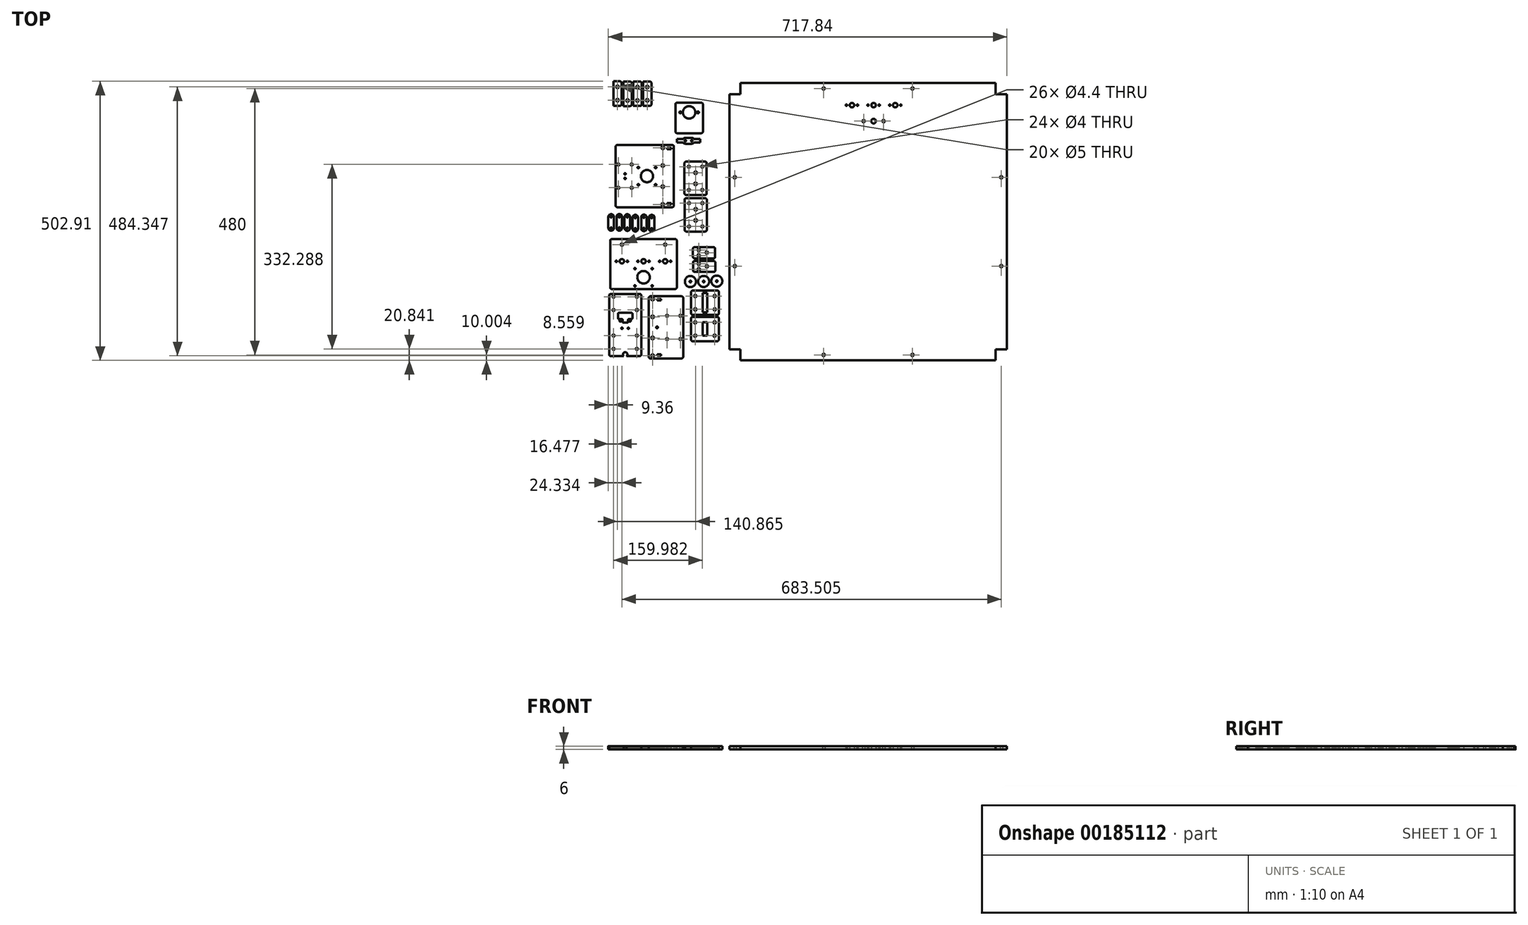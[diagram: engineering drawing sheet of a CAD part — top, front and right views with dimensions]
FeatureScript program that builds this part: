
annotation { "Feature Type Name" : "Feature", "Feature Type Description" : "" }
export const myFeature = defineFeature(function(context is Context, id is Id, definition is map)
    precondition{}
    {
        {
            var Q0;
            Q0=qCreatedBy(makeId("Top.planeOp"),FACE);
            var sketch = newSketch(context, id + "F0", { "sketchPlane" : qUnion([Q0])});
            skLineSegment(sketch, "E0.bottom", {"start": v(-220.47, 123.7) * mm, "end": v(-121.47, 123.7) * mm});
            skLineSegment(sketch, "E0.top", {"start": v(-220.47, 11.7) * mm, "end": v(-121.47, 11.7) * mm});
            skLineSegment(sketch, "E0.left", {"start": v(-223.47, 120.7) * mm, "end": v(-223.47, 14.7) * mm});
            skLineSegment(sketch, "E0.right", {"start": v(-118.47, 120.7) * mm, "end": v(-118.47, 14.7) * mm});
            skCircle(sketch, "E1", {"center": v(-218.47, 88.7) * mm, "radius": 2 * mm});
            skCircle(sketch, "E2", {"center": v(-218.47, 46.7) * mm, "radius": 2 * mm});
            skCircle(sketch, "E3", {"center": v(-194.47, 88.7) * mm, "radius": 2 * mm});
            skCircle(sketch, "E4", {"center": v(-182.47, 83.2) * mm, "radius": 1.4 * mm});
            skCircle(sketch, "E5", {"center": v(-151.47, 83.2) * mm, "radius": 1.4 * mm});
            skCircle(sketch, "E6", {"center": v(-151.47, 52.2) * mm, "radius": 1.4 * mm});
            skCircle(sketch, "E7", {"center": v(-182.47, 52.2) * mm, "radius": 1.4 * mm});
            skCircle(sketch, "E8", {"center": v(-166.97, 67.7) * mm, "radius": 11.1 * mm});
            skCircle(sketch, "E9", {"center": v(-194.47, 46.7) * mm, "radius": 2 * mm});
            skCircle(sketch, "E10", {"center": v(-138.47, 118.7) * mm, "radius": 2.5 * mm});
            skCircle(sketch, "E11", {"center": v(-138.47, 86.7) * mm, "radius": 2.5 * mm});
            skCircle(sketch, "E12", {"center": v(-138.47, 48.7) * mm, "radius": 2.5 * mm});
            skCircle(sketch, "E13", {"center": v(-138.47, 16.7) * mm, "radius": 2.5 * mm});
            skCircle(sketch, "E14", {"center": v(-206.47, 71.7) * mm, "radius": 1.3 * mm});
            skCircle(sketch, "E15", {"center": v(-206.47, 63.7) * mm, "radius": 1.3 * mm});
            skLineSegment(sketch, "E16.bottom", {"start": v(-130.47, 118.7) * mm, "end": v(-123.47, 118.7) * mm});
            skLineSegment(sketch, "E16.top", {"start": v(-130.47, 116.2) * mm, "end": v(-123.47, 116.2) * mm});
            skLineSegment(sketch, "E16.left", {"start": v(-130.47, 118.7) * mm, "end": v(-130.47, 116.2) * mm});
            skLineSegment(sketch, "E16.right", {"start": v(-123.47, 118.7) * mm, "end": v(-123.47, 116.2) * mm});
            skLineSegment(sketch, "E17.bottom", {"start": v(-130.47, 19.2) * mm, "end": v(-123.47, 19.2) * mm});
            skLineSegment(sketch, "E17.top", {"start": v(-130.47, 16.7) * mm, "end": v(-123.47, 16.7) * mm});
            skLineSegment(sketch, "E17.left", {"start": v(-130.47, 19.2) * mm, "end": v(-130.47, 16.7) * mm});
            skLineSegment(sketch, "E17.right", {"start": v(-123.47, 19.2) * mm, "end": v(-123.47, 16.7) * mm});
            skPoint(sketch, "E18.visualSharp", {"position": v(-118.47, 123.7) * mm});
            skArc(sketch, "E18.filletArc", {"start": v(-118.47, 120.7) * mm, "mid": v(-119.35, 122.83) * mm, "end": v(-121.47, 123.7) * mm});
            skPoint(sketch, "E19.visualSharp", {"position": v(-223.47, 123.7) * mm});
            skArc(sketch, "E19.filletArc", {"start": v(-220.47, 123.7) * mm, "mid": v(-222.6, 122.83) * mm, "end": v(-223.47, 120.7) * mm});
            skPoint(sketch, "E20.visualSharp", {"position": v(-223.47, 11.7) * mm});
            skArc(sketch, "E20.filletArc", {"start": v(-223.47, 14.7) * mm, "mid": v(-222.6, 12.59) * mm, "end": v(-220.47, 11.7) * mm});
            skPoint(sketch, "E21.visualSharp", {"position": v(-118.47, 11.7) * mm});
            skArc(sketch, "E21.filletArc", {"start": v(-121.47, 11.7) * mm, "mid": v(-119.35, 12.59) * mm, "end": v(-118.47, 14.7) * mm});
            skSolve(sketch);
        }
        {
            var Q0;
            Q0 = qSketchRegion(id + "F0", true);
            extrude(context, id + "F1", {"entities" : qUnion([Q0]), "depth" : 6 * mm});
        }
        {
            var Q0;
            Q0=qCreatedBy(makeId("Top.planeOp"),FACE);
            var sketch = newSketch(context, id + "F2", { "sketchPlane" : qUnion([Q0])});
            skLineSegment(sketch, "E22.bottom", {"start": v(127.2, 102.14) * mm, "end": v(183.2, 102.14) * mm});
            skLineSegment(sketch, "E22.top", {"start": v(127.2, -9.86) * mm, "end": v(183.2, -9.86) * mm});
            skLineSegment(sketch, "E22.left", {"start": v(124.2, 99.14) * mm, "end": v(124.2, -6.86) * mm});
            skLineSegment(sketch, "E22.right", {"start": v(186.2, 99.14) * mm, "end": v(186.2, -6.86) * mm});
            skCircle(sketch, "E23", {"center": v(157.2, 67.14) * mm, "radius": 2 * mm});
            skCircle(sketch, "E24", {"center": v(157.2, 25.14) * mm, "radius": 2 * mm});
            skCircle(sketch, "E25", {"center": v(181.2, 67.14) * mm, "radius": 2 * mm});
            skCircle(sketch, "E26", {"center": v(181.2, 25.14) * mm, "radius": 2 * mm});
            skCircle(sketch, "E27", {"center": v(131.2, 97.14) * mm, "radius": 2.5 * mm});
            skCircle(sketch, "E28", {"center": v(131.2, 65.14) * mm, "radius": 2.5 * mm});
            skCircle(sketch, "E29", {"center": v(131.2, 27.14) * mm, "radius": 2.5 * mm});
            skCircle(sketch, "E30", {"center": v(131.2, -4.86) * mm, "radius": 2.5 * mm});
            skLineSegment(sketch, "E31.bottom", {"start": v(139.2, 97.14) * mm, "end": v(146.2, 97.14) * mm});
            skLineSegment(sketch, "E31.top", {"start": v(139.2, 94.64) * mm, "end": v(146.2, 94.64) * mm});
            skLineSegment(sketch, "E31.left", {"start": v(139.2, 97.14) * mm, "end": v(139.2, 94.64) * mm});
            skLineSegment(sketch, "E31.right", {"start": v(146.2, 97.14) * mm, "end": v(146.2, 94.64) * mm});
            skLineSegment(sketch, "E32.bottom", {"start": v(139.2, -2.36) * mm, "end": v(146.2, -2.36) * mm});
            skLineSegment(sketch, "E32.top", {"start": v(139.2, -4.86) * mm, "end": v(146.2, -4.86) * mm});
            skLineSegment(sketch, "E32.left", {"start": v(139.2, -2.36) * mm, "end": v(139.2, -4.86) * mm});
            skLineSegment(sketch, "E32.right", {"start": v(146.2, -2.36) * mm, "end": v(146.2, -4.86) * mm});
            skPoint(sketch, "E33.visualSharp", {"position": v(124.2, 102.14) * mm});
            skArc(sketch, "E33.filletArc", {"start": v(127.2, 102.14) * mm, "mid": v(125.08, 101.26) * mm, "end": v(124.2, 99.14) * mm});
            skPoint(sketch, "E34.visualSharp", {"position": v(186.2, 102.14) * mm});
            skArc(sketch, "E34.filletArc", {"start": v(186.2, 99.14) * mm, "mid": v(185.32, 101.26) * mm, "end": v(183.2, 102.14) * mm});
            skPoint(sketch, "E35.visualSharp", {"position": v(186.2, -9.86) * mm});
            skArc(sketch, "E35.filletArc", {"start": v(183.2, -9.86) * mm, "mid": v(185.32, -8.98) * mm, "end": v(186.2, -6.86) * mm});
            skPoint(sketch, "E36.visualSharp", {"position": v(124.2, -9.86) * mm});
            skArc(sketch, "E36.filletArc", {"start": v(124.2, -6.86) * mm, "mid": v(125.08, -8.98) * mm, "end": v(127.2, -9.86) * mm});
            skCircle(sketch, "E37", {"center": v(139.2, 46.14) * mm, "radius": 1.5 * mm});
            skSolve(sketch);
        }
        {
            var Q0;
            Q0 = qSketchRegion(id + "F2", true);
            extrude(context, id + "F3", {"entities" : qUnion([Q0]), "depth" : 6 * mm});
        }
        {
            var Q0;
            Q0=qCreatedBy(makeId("Top.planeOp"),FACE);
            var sketch = newSketch(context, id + "F4", { "sketchPlane" : qUnion([Q0])});
            skLineSegment(sketch, "E38.bottom", {"start": v(-34.17, 117.42) * mm, "end": v(17.83, 117.42) * mm});
            skLineSegment(sketch, "E38.top", {"start": v(-34.17, 5.42) * mm, "end": v(-10.82, 5.42) * mm});
            skLineSegment(sketch, "E38.left", {"start": v(-37.17, 114.42) * mm, "end": v(-37.17, 8.42) * mm});
            skLineSegment(sketch, "E38.right", {"start": v(20.83, 114.42) * mm, "end": v(20.83, 67.93) * mm});
            skCircle(sketch, "E39", {"center": v(-29.17, 112.42) * mm, "radius": 2 * mm});
            skCircle(sketch, "E40", {"center": v(-29.17, 88.42) * mm, "radius": 2 * mm});
            skCircle(sketch, "E41", {"center": v(12.83, 112.42) * mm, "radius": 2 * mm});
            skCircle(sketch, "E42", {"center": v(12.83, 88.42) * mm, "radius": 2 * mm});
            skCircle(sketch, "E43", {"center": v(-29.17, 42.42) * mm, "radius": 2 * mm});
            skCircle(sketch, "E44", {"center": v(-29.17, 18.42) * mm, "radius": 2 * mm});
            skCircle(sketch, "E45", {"center": v(12.83, 42.42) * mm, "radius": 2 * mm});
            skCircle(sketch, "E46", {"center": v(12.83, 18.42) * mm, "radius": 2 * mm});
            skCircle(sketch, "E47", {"center": v(-16.97, 68.92) * mm, "radius": 1.5 * mm});
            skCircle(sketch, "E48", {"center": v(0.63, 68.92) * mm, "radius": 1.5 * mm});
            skLineSegment(sketch, "E49.bottom", {"start": v(-19.17, 83.42) * mm, "end": v(2.83, 83.42) * mm});
            skLineSegment(sketch, "E49.top", {"start": v(-19.17, 71.92) * mm, "end": v(-13.97, 71.92) * mm});
            skLineSegment(sketch, "E49.left", {"start": v(-21.17, 81.42) * mm, "end": v(-21.17, 73.92) * mm});
            skLineSegment(sketch, "E49.right", {"start": v(4.83, 81.42) * mm, "end": v(4.83, 73.92) * mm});
            skPoint(sketch, "E50.visualSharp", {"position": v(-37.17, 117.42) * mm});
            skArc(sketch, "E50.filletArc", {"start": v(-34.17, 117.42) * mm, "mid": v(-36.3, 116.54) * mm, "end": v(-37.17, 114.42) * mm});
            skPoint(sketch, "E51.visualSharp", {"position": v(20.83, 117.42) * mm});
            skArc(sketch, "E51.filletArc", {"start": v(20.83, 114.42) * mm, "mid": v(19.95, 116.54) * mm, "end": v(17.83, 117.42) * mm});
            skPoint(sketch, "E52.visualSharp", {"position": v(20.83, 5.42) * mm});
            skArc(sketch, "E52.filletArc", {"start": v(17.83, 5.42) * mm, "mid": v(19.95, 6.3) * mm, "end": v(20.83, 8.42) * mm});
            skPoint(sketch, "E53.visualSharp", {"position": v(-37.17, 5.42) * mm});
            skArc(sketch, "E53.filletArc", {"start": v(-37.17, 8.42) * mm, "mid": v(-36.3, 6.3) * mm, "end": v(-34.17, 5.42) * mm});
            skPoint(sketch, "E54.visualSharp", {"position": v(4.83, 83.42) * mm});
            skArc(sketch, "E54.filletArc", {"start": v(4.83, 81.42) * mm, "mid": v(4.24, 82.84) * mm, "end": v(2.83, 83.42) * mm});
            skPoint(sketch, "E55.visualSharp", {"position": v(4.83, 71.92) * mm});
            skArc(sketch, "E55.filletArc", {"start": v(2.83, 71.92) * mm, "mid": v(4.24, 72.5) * mm, "end": v(4.83, 73.92) * mm});
            skPoint(sketch, "E56.visualSharp", {"position": v(-21.17, 71.92) * mm});
            skArc(sketch, "E56.filletArc", {"start": v(-21.17, 73.92) * mm, "mid": v(-20.58, 72.5) * mm, "end": v(-19.17, 71.92) * mm});
            skPoint(sketch, "E57.visualSharp", {"position": v(-21.17, 83.42) * mm});
            skArc(sketch, "E57.filletArc", {"start": v(-19.17, 83.42) * mm, "mid": v(-20.58, 82.84) * mm, "end": v(-21.17, 81.42) * mm});
            skCircle(sketch, "E58", {"center": v(-13.97, 55.42) * mm, "radius": 1.3 * mm});
            skCircle(sketch, "E59", {"center": v(-2.37, 55.42) * mm, "radius": 1.3 * mm});
            skLineSegment(sketch, "E60.trimOffspring", {"start": v(20.83, 59.08) * mm, "end": v(20.83, 8.42) * mm});
            skLineSegment(sketch, "E61.top", {"start": v(-11.97, 65.92) * mm, "end": v(-3.97, 65.92) * mm});
            skLineSegment(sketch, "E61.left", {"start": v(-12.97, 70.92) * mm, "end": v(-12.97, 66.92) * mm});
            skLineSegment(sketch, "E61.right", {"start": v(-2.97, 70.92) * mm, "end": v(-2.97, 66.92) * mm});
            skLineSegment(sketch, "E62.trimOffspring", {"start": v(-1.97, 71.92) * mm, "end": v(2.83, 71.92) * mm});
            skPoint(sketch, "E63.visualSharp", {"position": v(-12.97, 71.92) * mm});
            skArc(sketch, "E63.filletArc", {"start": v(-12.97, 70.92) * mm, "mid": v(-13.26, 71.63) * mm, "end": v(-13.97, 71.92) * mm});
            skPoint(sketch, "E64.visualSharp", {"position": v(-2.97, 71.92) * mm});
            skArc(sketch, "E64.filletArc", {"start": v(-1.97, 71.92) * mm, "mid": v(-2.68, 71.63) * mm, "end": v(-2.97, 70.92) * mm});
            skPoint(sketch, "E65.visualSharp", {"position": v(-12.97, 65.92) * mm});
            skArc(sketch, "E65.filletArc", {"start": v(-12.97, 66.92) * mm, "mid": v(-12.68, 66.21) * mm, "end": v(-11.97, 65.92) * mm});
            skPoint(sketch, "E66.visualSharp", {"position": v(-2.97, 65.92) * mm});
            skArc(sketch, "E66.filletArc", {"start": v(-3.97, 65.92) * mm, "mid": v(-3.26, 66.21) * mm, "end": v(-2.97, 66.92) * mm});
            skLineSegment(sketch, "E67", {"start": v(20.83, 59.08) * mm, "end": v(20.83, 67.93) * mm});
            skArc(sketch, "E68", {"start": v(-5.52, 5.42) * mm, "mid": v(-8.17, 12.42) * mm, "end": v(-10.82, 5.42) * mm});
            skPoint(sketch, "E68.centerSnap0", {"position": v(-8.17, 5.42) * mm});
            skLineSegment(sketch, "E69.trimOffspring", {"start": v(-5.52, 5.42) * mm, "end": v(17.83, 5.42) * mm});
            skSolve(sketch);
        }
        {
            var Q0;
            Q0=makeQuery(id+"F4.imprint","IMPRINT",FACE,{"disambiguationData":[TD([[makeQuery(id+"F4.imprint","IMPRINT",EDGE,{"derivedFrom":sQuery(id+"F4.wireOp",EDGE,"E38.bottom")}),-1.0]])]});
            extrude(context, id + "F5", {"entities" : qUnion([Q0]), "depth" : 6 * mm});
        }
        {
            var Q0;
            Q0=qCreatedBy(makeId("Top.planeOp"),FACE);
            var sketch = newSketch(context, id + "F6", { "sketchPlane" : qUnion([Q0])});
            skLineSegment(sketch, "E70.bottom", {"start": v(-96.37, 93.78) * mm, "end": v(-62.37, 93.78) * mm});
            skLineSegment(sketch, "E70.top", {"start": v(-96.37, 33.78) * mm, "end": v(-62.37, 33.78) * mm});
            skLineSegment(sketch, "E70.left", {"start": v(-99.37, 90.78) * mm, "end": v(-99.37, 36.78) * mm});
            skLineSegment(sketch, "E70.right", {"start": v(-59.37, 90.78) * mm, "end": v(-59.37, 36.78) * mm});
            skCircle(sketch, "E71", {"center": v(-91.37, 84.78) * mm, "radius": 2 * mm});
            skCircle(sketch, "E72", {"center": v(-67.37, 84.78) * mm, "radius": 2 * mm});
            skCircle(sketch, "E73", {"center": v(-91.37, 42.78) * mm, "radius": 2 * mm});
            skCircle(sketch, "E74", {"center": v(-67.37, 42.78) * mm, "radius": 2 * mm});
            skCircle(sketch, "E75", {"center": v(-79.37, 73.78) * mm, "radius": 2.5 * mm});
            skCircle(sketch, "E76", {"center": v(-79.37, 53.78) * mm, "radius": 2.5 * mm});
            skPoint(sketch, "E77.visualSharp", {"position": v(-99.37, 93.78) * mm});
            skArc(sketch, "E77.filletArc", {"start": v(-96.37, 93.78) * mm, "mid": v(-98.49, 92.9) * mm, "end": v(-99.37, 90.78) * mm});
            skPoint(sketch, "E78.visualSharp", {"position": v(-59.37, 93.78) * mm});
            skArc(sketch, "E78.filletArc", {"start": v(-59.37, 90.78) * mm, "mid": v(-60.24, 92.9) * mm, "end": v(-62.37, 93.78) * mm});
            skPoint(sketch, "E79.visualSharp", {"position": v(-59.37, 33.78) * mm});
            skArc(sketch, "E79.filletArc", {"start": v(-62.37, 33.78) * mm, "mid": v(-60.24, 34.65) * mm, "end": v(-59.37, 36.78) * mm});
            skPoint(sketch, "E80.visualSharp", {"position": v(-99.37, 33.78) * mm});
            skArc(sketch, "E80.filletArc", {"start": v(-99.37, 36.78) * mm, "mid": v(-98.49, 34.65) * mm, "end": v(-96.37, 33.78) * mm});
            skSolve(sketch);
        }
        {
            var Q0;
            Q0 = qSketchRegion(id + "F6", true);
            extrude(context, id + "F7", {"entities" : qUnion([Q0]), "depth" : 6 * mm});
        }
        {
            var Q0;
            Q0=qCreatedBy(makeId("Top.planeOp"),FACE);
            var sketch = newSketch(context, id + "F8", { "sketchPlane" : qUnion([Q0])});
            skLineSegment(sketch, "E81.bottom", {"start": v(-96.19, 27.94) * mm, "end": v(-62.19, 27.94) * mm});
            skLineSegment(sketch, "E81.top", {"start": v(-96.19, -32.06) * mm, "end": v(-62.19, -32.06) * mm});
            skLineSegment(sketch, "E81.left", {"start": v(-99.19, 24.94) * mm, "end": v(-99.19, -29.06) * mm});
            skLineSegment(sketch, "E81.right", {"start": v(-59.19, 24.94) * mm, "end": v(-59.19, -29.06) * mm});
            skCircle(sketch, "E82", {"center": v(-91.19, 18.94) * mm, "radius": 2 * mm});
            skCircle(sketch, "E83", {"center": v(-67.19, 18.94) * mm, "radius": 2 * mm});
            skCircle(sketch, "E84", {"center": v(-91.19, -23.06) * mm, "radius": 2 * mm});
            skCircle(sketch, "E85", {"center": v(-67.19, -23.06) * mm, "radius": 2 * mm});
            skCircle(sketch, "E86", {"center": v(-79.19, 7.94) * mm, "radius": 2.5 * mm});
            skCircle(sketch, "E87", {"center": v(-79.19, -12.06) * mm, "radius": 2.5 * mm});
            skPoint(sketch, "E88.visualSharp", {"position": v(-99.19, 27.94) * mm});
            skArc(sketch, "E88.filletArc", {"start": v(-96.19, 27.94) * mm, "mid": v(-98.3, 27.06) * mm, "end": v(-99.19, 24.94) * mm});
            skPoint(sketch, "E89.visualSharp", {"position": v(-59.19, 27.94) * mm});
            skArc(sketch, "E89.filletArc", {"start": v(-59.19, 24.94) * mm, "mid": v(-60.07, 27.06) * mm, "end": v(-62.19, 27.94) * mm});
            skPoint(sketch, "E90.visualSharp", {"position": v(-59.19, -32.06) * mm});
            skArc(sketch, "E90.filletArc", {"start": v(-62.19, -32.06) * mm, "mid": v(-60.07, -31.19) * mm, "end": v(-59.19, -29.06) * mm});
            skPoint(sketch, "E91.visualSharp", {"position": v(-99.19, -32.06) * mm});
            skArc(sketch, "E91.filletArc", {"start": v(-99.19, -29.06) * mm, "mid": v(-98.3, -31.19) * mm, "end": v(-96.19, -32.06) * mm});
            skSolve(sketch);
        }
        {
            var Q0;
            Q0 = qSketchRegion(id + "F8", true);
            extrude(context, id + "F9", {"entities" : qUnion([Q0]), "depth" : 6 * mm});
        }
        {
            var Q0;
            Q0=qCreatedBy(makeId("Top.planeOp"),FACE);
            var sketch = newSketch(context, id + "F10", { "sketchPlane" : qUnion([Q0])});
            skLineSegment(sketch, "E92.bottom", {"start": v(48.83, 100.6) * mm, "end": v(82.83, 100.6) * mm});
            skLineSegment(sketch, "E92.top", {"start": v(48.83, 80.6) * mm, "end": v(82.83, 80.6) * mm});
            skLineSegment(sketch, "E92.left", {"start": v(45.83, 97.6) * mm, "end": v(45.83, 83.6) * mm});
            skLineSegment(sketch, "E92.right", {"start": v(85.83, 97.6) * mm, "end": v(85.83, 83.6) * mm});
            skPoint(sketch, "E93.visualSharp", {"position": v(45.83, 100.6) * mm});
            skArc(sketch, "E93.filletArc", {"start": v(48.83, 100.6) * mm, "mid": v(46.7, 99.72) * mm, "end": v(45.83, 97.6) * mm});
            skPoint(sketch, "E94.visualSharp", {"position": v(45.83, 80.6) * mm});
            skArc(sketch, "E94.filletArc", {"start": v(45.83, 83.6) * mm, "mid": v(46.7, 81.48) * mm, "end": v(48.83, 80.6) * mm});
            skPoint(sketch, "E95.visualSharp", {"position": v(85.83, 80.6) * mm});
            skArc(sketch, "E95.filletArc", {"start": v(82.83, 80.6) * mm, "mid": v(84.95, 81.48) * mm, "end": v(85.83, 83.6) * mm});
            skPoint(sketch, "E96.visualSharp", {"position": v(85.83, 100.6) * mm});
            skArc(sketch, "E96.filletArc", {"start": v(85.83, 97.6) * mm, "mid": v(84.95, 99.72) * mm, "end": v(82.83, 100.6) * mm});
            skPoint(sketch, "E97", {"position": v(70.83, 90.83) * mm});
            skPoint(sketch, "E98", {"position": v(56.26, 95.6) * mm});
            skPoint(sketch, "E99", {"position": v(56.26, 85.6) * mm});
            skSolve(sketch);
        }
        {
            var Q0;
            Q0 = qSketchRegion(id + "F10", true);
            extrude(context, id + "F11", {"entities" : qUnion([Q0]), "depth" : 6 * mm});
        }
        {
            var Q0;
            Q0=sQuery(id+"F10.wireOp",VERTEX,"E97");
            var Q1;
            Q1=sQuery(id+"F10.wireOp",VERTEX,"E98");
            var Q2;
            Q2=sQuery(id+"F10.wireOp",VERTEX,"E99");
            var Q3;
            Q3=makeQuery(id+"F11.opExtrude","SWEPT_BODY",BODY,{"disambiguationData":[OSD([sQuery(id+"F10.wireOp",EDGE,"E92.bottom"),sQuery(id+"F10.wireOp",EDGE,"E92.top"),sQuery(id+"F10.wireOp",EDGE,"E92.left"),sQuery(id+"F10.wireOp",EDGE,"E92.right"),sQuery(id+"F10.wireOp",EDGE,"E93.filletArc"),sQuery(id+"F10.wireOp",EDGE,"E94.filletArc"),sQuery(id+"F10.wireOp",EDGE,"E95.filletArc"),sQuery(id+"F10.wireOp",EDGE,"E96.filletArc")])]});
            hole(context, id + "F12", {"style" : HoleStyle.SIMPLE, "endStyle" : HoleEndStyle.THROUGH, "oppositeDirection" : true, "standardTappedOrClearance" : lookupTablePath({ "standard" : "ISO", "engagement" : "25%", "pitch" : "0.9 mm", "size" : "M5", "type" : "Tapped" }), "standardBlindInLast" : lookupTablePath({ "standard" : "ISO", "engagement" : "25%", "pitch" : "0.9 mm", "size" : "M5", "type" : "Tapped" }), "holeDiameter" : 4.4 * mm, "locations" : qUnion([Q0, Q1, Q2]), "scope" : qUnion([Q3]), "isTappedThrough" : true, "showTappedDepth" : true});
        }
        {
            var Q0;
            Q0=qCreatedBy(makeId("Top.planeOp"),FACE);
            var sketch = newSketch(context, id + "F13", { "sketchPlane" : qUnion([Q0])});
            skLineSegment(sketch, "E100.bottom", {"start": v(49.04, 75.93) * mm, "end": v(83.04, 75.93) * mm});
            skLineSegment(sketch, "E100.top", {"start": v(49.04, 55.93) * mm, "end": v(83.04, 55.93) * mm});
            skLineSegment(sketch, "E100.left", {"start": v(46.04, 72.93) * mm, "end": v(46.04, 58.93) * mm});
            skLineSegment(sketch, "E100.right", {"start": v(86.04, 72.93) * mm, "end": v(86.04, 58.93) * mm});
            skPoint(sketch, "E101.visualSharp", {"position": v(46.04, 75.93) * mm});
            skArc(sketch, "E101.filletArc", {"start": v(49.04, 75.93) * mm, "mid": v(46.92, 75.05) * mm, "end": v(46.04, 72.93) * mm});
            skPoint(sketch, "E102.visualSharp", {"position": v(46.04, 55.93) * mm});
            skArc(sketch, "E102.filletArc", {"start": v(46.04, 58.93) * mm, "mid": v(46.92, 56.81) * mm, "end": v(49.04, 55.93) * mm});
            skPoint(sketch, "E103.visualSharp", {"position": v(86.04, 55.93) * mm});
            skArc(sketch, "E103.filletArc", {"start": v(83.04, 55.93) * mm, "mid": v(85.16, 56.81) * mm, "end": v(86.04, 58.93) * mm});
            skPoint(sketch, "E104.visualSharp", {"position": v(86.04, 75.93) * mm});
            skArc(sketch, "E104.filletArc", {"start": v(86.04, 72.93) * mm, "mid": v(85.16, 75.05) * mm, "end": v(83.04, 75.93) * mm});
            skPoint(sketch, "E105", {"position": v(71.04, 66.17) * mm});
            skPoint(sketch, "E106", {"position": v(56.47, 70.93) * mm});
            skPoint(sketch, "E107", {"position": v(56.47, 60.93) * mm});
            skSolve(sketch);
        }
        {
            var Q0;
            Q0=makeQuery(id+"F13.imprint","IMPRINT",FACE,{"disambiguationData":[TD([[makeQuery(id+"F13.imprint","IMPRINT",EDGE,{"derivedFrom":sQuery(id+"F13.wireOp",EDGE,"E100.bottom")}),-1.0]])]});
            extrude(context, id + "F14", {"entities" : qUnion([Q0]), "depth" : 6 * mm});
        }
        {
            var Q0;
            Q0=sQuery(id+"F13.wireOp",VERTEX,"E106");
            var Q1;
            Q1=sQuery(id+"F13.wireOp",VERTEX,"E107");
            var Q2;
            Q2=sQuery(id+"F13.wireOp",VERTEX,"E105");
            var Q3;
            Q3=makeQuery(id+"F14.opExtrude","SWEPT_BODY",BODY,{"disambiguationData":[OSD([sQuery(id+"F13.wireOp",EDGE,"E100.bottom"),sQuery(id+"F13.wireOp",EDGE,"E100.top"),sQuery(id+"F13.wireOp",EDGE,"E100.left"),sQuery(id+"F13.wireOp",EDGE,"E100.right"),sQuery(id+"F13.wireOp",EDGE,"E101.filletArc"),sQuery(id+"F13.wireOp",EDGE,"E102.filletArc"),sQuery(id+"F13.wireOp",EDGE,"E103.filletArc"),sQuery(id+"F13.wireOp",EDGE,"E104.filletArc")])]});
            hole(context, id + "F15", {"style" : HoleStyle.SIMPLE, "endStyle" : HoleEndStyle.THROUGH, "oppositeDirection" : true, "standardTappedOrClearance" : lookupTablePath({ "standard" : "ISO", "engagement" : "25%", "pitch" : "0.9 mm", "size" : "M5", "type" : "Tapped" }), "standardBlindInLast" : lookupTablePath({ "standard" : "ISO", "engagement" : "25%", "pitch" : "0.9 mm", "size" : "M5", "type" : "Tapped" }), "holeDiameter" : 4.4 * mm, "locations" : qUnion([Q0, Q1, Q2]), "scope" : qUnion([Q3]), "isTappedThrough" : true, "showTappedDepth" : true});
        }
        {
            var Q0;
            Q0=qCreatedBy(makeId("Top.planeOp"),FACE);
            var sketch = newSketch(context, id + "F16", { "sketchPlane" : qUnion([Q0])});
            skCircle(sketch, "E108", {"center": v(41.35, 38.74) * mm, "radius": 10 * mm});
            skSolve(sketch);
        }
        {
            var Q0;
            Q0=makeQuery(id+"F16.imprint","IMPRINT",FACE,{"disambiguationData":[TD([[makeQuery(id+"F16.imprint","IMPRINT",EDGE,{"derivedFrom":sQuery(id+"F16.wireOp",EDGE,"E108")}),1.0]])]});
            extrude(context, id + "F17", {"entities" : qUnion([Q0]), "depth" : 6 * mm});
        }
        {
            var Q0;
            Q0=sQuery(id+"F16.wireOp",VERTEX,"E108.center");
            var Q1;
            Q1=makeQuery(id+"F17.opExtrude","SWEPT_BODY",BODY,{"disambiguationData":[OSD([sQuery(id+"F16.wireOp",EDGE,"E108")])]});
            hole(context, id + "F18", {"style" : HoleStyle.SIMPLE, "endStyle" : HoleEndStyle.THROUGH, "oppositeDirection" : true, "standardTappedOrClearance" : lookupTablePath({ "standard" : "ISO", "size" : "3", "type" : "Drilled" }), "standardBlindInLast" : lookupTablePath({ "standard" : "ISO", "size" : "3", "type" : "Drilled" }), "holeDiameter" : 3 * mm, "locations" : qUnion([Q0]), "scope" : qUnion([Q1]), "tappedDepth" : 12 * mm, "tapClearance" : 3});
        }
        {
            var Q0;
            Q0=qCreatedBy(makeId("Top.planeOp"),FACE);
            var sketch = newSketch(context, id + "F19", { "sketchPlane" : qUnion([Q0])});
            skCircle(sketch, "E109", {"center": v(65.18, 38.92) * mm, "radius": 10 * mm});
            skSolve(sketch);
        }
        {
            var Q0;
            Q0=makeQuery(id+"F19.imprint","IMPRINT",FACE,{"disambiguationData":[TD([[makeQuery(id+"F19.imprint","IMPRINT",EDGE,{"derivedFrom":sQuery(id+"F19.wireOp",EDGE,"E109")}),1.0]])]});
            extrude(context, id + "F20", {"entities" : qUnion([Q0]), "depth" : 6 * mm});
        }
        {
            var Q0;
            Q0=sQuery(id+"F19.wireOp",VERTEX,"E109.center");
            var Q1;
            Q1=makeQuery(id+"F20.opExtrude","SWEPT_BODY",BODY,{"disambiguationData":[OSD([sQuery(id+"F19.wireOp",EDGE,"E109")])]});
            hole(context, id + "F21", {"style" : HoleStyle.SIMPLE, "endStyle" : HoleEndStyle.THROUGH, "oppositeDirection" : true, "standardTappedOrClearance" : lookupTablePath({ "standard" : "ISO", "size" : "3", "type" : "Drilled" }), "standardBlindInLast" : lookupTablePath({ "standard" : "ISO", "size" : "3", "type" : "Drilled" }), "holeDiameter" : 3 * mm, "locations" : qUnion([Q0]), "scope" : qUnion([Q1]), "tappedDepth" : 12 * mm, "tapClearance" : 3});
        }
        {
            var Q0;
            Q0=qCreatedBy(makeId("Top.planeOp"),FACE);
            var sketch = newSketch(context, id + "F22", { "sketchPlane" : qUnion([Q0])});
            skCircle(sketch, "E110", {"center": v(88.79, 39.55) * mm, "radius": 10 * mm});
            skSolve(sketch);
        }
        {
            var Q0;
            Q0=makeQuery(id+"F22.imprint","IMPRINT",FACE,{"disambiguationData":[TD([[makeQuery(id+"F22.imprint","IMPRINT",EDGE,{"derivedFrom":sQuery(id+"F22.wireOp",EDGE,"E110")}),1.0]])]});
            extrude(context, id + "F23", {"entities" : qUnion([Q0]), "depth" : 6 * mm});
        }
        {
            var Q0;
            Q0=sQuery(id+"F22.wireOp",VERTEX,"E110.center");
            var Q1;
            Q1=makeQuery(id+"F23.opExtrude","SWEPT_BODY",BODY,{"disambiguationData":[OSD([sQuery(id+"F22.wireOp",EDGE,"E110")])]});
            hole(context, id + "F24", {"style" : HoleStyle.SIMPLE, "endStyle" : HoleEndStyle.THROUGH, "oppositeDirection" : true, "standardTappedOrClearance" : lookupTablePath({ "standard" : "ISO", "size" : "3", "type" : "Drilled" }), "standardBlindInLast" : lookupTablePath({ "standard" : "ISO", "size" : "3", "type" : "Drilled" }), "holeDiameter" : 3 * mm, "locations" : qUnion([Q0]), "scope" : qUnion([Q1]), "tappedDepth" : 12 * mm, "tapClearance" : 3});
        }
        {
            var Q0;
            Q0=qCreatedBy(makeId("Top.planeOp"),FACE);
            var sketch = newSketch(context, id + "F25", { "sketchPlane" : qUnion([Q0])});
            skLineSegment(sketch, "E111.bottom", {"start": v(45.6, 22.62) * mm, "end": v(89.6, 22.62) * mm});
            skLineSegment(sketch, "E111.top", {"start": v(45.6, -21.38) * mm, "end": v(89.6, -21.38) * mm});
            skLineSegment(sketch, "E111.left", {"start": v(42.6, 19.62) * mm, "end": v(42.6, -18.38) * mm});
            skLineSegment(sketch, "E111.right", {"start": v(92.6, 19.62) * mm, "end": v(92.6, -18.38) * mm});
            skPoint(sketch, "E112", {"position": v(50.1, 12.62) * mm});
            skPoint(sketch, "E113", {"position": v(50.1, -11.38) * mm});
            skPoint(sketch, "E114", {"position": v(85.1, -11.38) * mm});
            skPoint(sketch, "E115", {"position": v(85.1, 12.62) * mm});
            skLineSegment(sketch, "E116.bottom", {"start": v(63.6, 18.22) * mm, "end": v(71.6, 18.22) * mm});
            skLineSegment(sketch, "E116.top", {"start": v(63.6, -16.98) * mm, "end": v(71.6, -16.98) * mm});
            skLineSegment(sketch, "E116.left", {"start": v(63.6, 18.22) * mm, "end": v(63.6, -16.98) * mm});
            skLineSegment(sketch, "E116.right", {"start": v(71.6, 18.22) * mm, "end": v(71.6, -16.98) * mm});
            skPoint(sketch, "E117.visualSharp", {"position": v(42.6, 22.62) * mm});
            skArc(sketch, "E117.filletArc", {"start": v(45.6, 22.62) * mm, "mid": v(43.49, 21.74) * mm, "end": v(42.6, 19.62) * mm});
            skPoint(sketch, "E118.visualSharp", {"position": v(42.6, -21.38) * mm});
            skArc(sketch, "E118.filletArc", {"start": v(42.6, -18.38) * mm, "mid": v(43.49, -20.5) * mm, "end": v(45.6, -21.38) * mm});
            skPoint(sketch, "E119.visualSharp", {"position": v(92.6, -21.38) * mm});
            skArc(sketch, "E119.filletArc", {"start": v(89.6, -21.38) * mm, "mid": v(91.73, -20.5) * mm, "end": v(92.6, -18.38) * mm});
            skPoint(sketch, "E120.visualSharp", {"position": v(92.6, 22.62) * mm});
            skArc(sketch, "E120.filletArc", {"start": v(92.6, 19.62) * mm, "mid": v(91.73, 21.74) * mm, "end": v(89.6, 22.62) * mm});
            skSolve(sketch);
        }
        {
            var Q0;
            Q0=makeQuery(id+"F25.imprint","IMPRINT",FACE,{"disambiguationData":[TD([[makeQuery(id+"F25.imprint","IMPRINT",EDGE,{"derivedFrom":sQuery(id+"F25.wireOp",EDGE,"E111.bottom")}),-1.0]])]});
            extrude(context, id + "F26", {"entities" : qUnion([Q0]), "depth" : 6 * mm});
        }
        {
            var Q0;
            Q0=sQuery(id+"F25.wireOp",VERTEX,"E112");
            var Q1;
            Q1=sQuery(id+"F25.wireOp",VERTEX,"E113");
            var Q2;
            Q2=sQuery(id+"F25.wireOp",VERTEX,"E115");
            var Q3;
            Q3=sQuery(id+"F25.wireOp",VERTEX,"E114");
            var Q4;
            Q4=makeQuery(id+"F26.opExtrude","SWEPT_BODY",BODY,{"disambiguationData":[OSD([sQuery(id+"F25.wireOp",EDGE,"E111.bottom"),sQuery(id+"F25.wireOp",EDGE,"E111.top"),sQuery(id+"F25.wireOp",EDGE,"E111.left"),sQuery(id+"F25.wireOp",EDGE,"E111.right"),sQuery(id+"F25.wireOp",EDGE,"E116.bottom"),sQuery(id+"F25.wireOp",EDGE,"E116.top"),sQuery(id+"F25.wireOp",EDGE,"E116.left"),sQuery(id+"F25.wireOp",EDGE,"E116.right"),sQuery(id+"F25.wireOp",EDGE,"E117.filletArc"),sQuery(id+"F25.wireOp",EDGE,"E118.filletArc"),sQuery(id+"F25.wireOp",EDGE,"E119.filletArc"),sQuery(id+"F25.wireOp",EDGE,"E120.filletArc")])]});
            hole(context, id + "F27", {"style" : HoleStyle.SIMPLE, "endStyle" : HoleEndStyle.THROUGH, "oppositeDirection" : true, "standardTappedOrClearance" : lookupTablePath({ "standard" : "ISO", "engagement" : "25%", "pitch" : "0.9 mm", "size" : "M5", "type" : "Tapped" }), "standardBlindInLast" : lookupTablePath({ "standard" : "ISO", "engagement" : "25%", "pitch" : "0.9 mm", "size" : "M5", "type" : "Tapped" }), "holeDiameter" : 4.4 * mm, "locations" : qUnion([Q0, Q1, Q2, Q3]), "scope" : qUnion([Q4]), "isTappedThrough" : true, "showTappedDepth" : true});
        }
        {
            var Q0;
            Q0=qCreatedBy(makeId("Top.planeOp"),FACE);
            var sketch = newSketch(context, id + "F28", { "sketchPlane" : qUnion([Q0])});
            skLineSegment(sketch, "E121.bottom", {"start": v(45.4, -24.84) * mm, "end": v(89.4, -24.84) * mm});
            skLineSegment(sketch, "E121.top", {"start": v(45.4, -68.84) * mm, "end": v(89.4, -68.84) * mm});
            skLineSegment(sketch, "E121.left", {"start": v(42.4, -27.84) * mm, "end": v(42.4, -65.84) * mm});
            skLineSegment(sketch, "E121.right", {"start": v(92.4, -27.84) * mm, "end": v(92.4, -65.84) * mm});
            skPoint(sketch, "E122", {"position": v(49.9, -34.84) * mm});
            skPoint(sketch, "E123", {"position": v(49.9, -58.84) * mm});
            skPoint(sketch, "E124", {"position": v(84.9, -58.84) * mm});
            skPoint(sketch, "E125", {"position": v(84.9, -34.84) * mm});
            skLineSegment(sketch, "E126.bottom", {"start": v(63.4, -34.74) * mm, "end": v(71.4, -34.74) * mm});
            skLineSegment(sketch, "E126.top", {"start": v(63.4, -58.94) * mm, "end": v(71.4, -58.94) * mm});
            skLineSegment(sketch, "E126.left", {"start": v(63.4, -34.74) * mm, "end": v(63.4, -58.94) * mm});
            skLineSegment(sketch, "E126.right", {"start": v(71.4, -34.74) * mm, "end": v(71.4, -58.94) * mm});
            skPoint(sketch, "E127.visualSharp", {"position": v(42.4, -24.84) * mm});
            skArc(sketch, "E127.filletArc", {"start": v(45.4, -24.84) * mm, "mid": v(43.28, -25.72) * mm, "end": v(42.4, -27.84) * mm});
            skPoint(sketch, "E128.visualSharp", {"position": v(42.4, -68.84) * mm});
            skArc(sketch, "E128.filletArc", {"start": v(42.4, -65.84) * mm, "mid": v(43.28, -67.96) * mm, "end": v(45.4, -68.84) * mm});
            skPoint(sketch, "E129.visualSharp", {"position": v(92.4, -68.84) * mm});
            skArc(sketch, "E129.filletArc", {"start": v(89.4, -68.84) * mm, "mid": v(91.53, -67.96) * mm, "end": v(92.4, -65.84) * mm});
            skPoint(sketch, "E130.visualSharp", {"position": v(92.4, -24.84) * mm});
            skArc(sketch, "E130.filletArc", {"start": v(92.4, -27.84) * mm, "mid": v(91.53, -25.72) * mm, "end": v(89.4, -24.84) * mm});
            skSolve(sketch);
        }
        {
            var Q0;
            Q0=makeQuery(id+"F28.imprint","IMPRINT",FACE,{"disambiguationData":[TD([[makeQuery(id+"F28.imprint","IMPRINT",EDGE,{"derivedFrom":sQuery(id+"F28.wireOp",EDGE,"E121.bottom")}),-1.0]])]});
            extrude(context, id + "F29", {"entities" : qUnion([Q0]), "depth" : 6 * mm});
        }
        {
            var Q0;
            Q0=sQuery(id+"F28.wireOp",VERTEX,"E122");
            var Q1;
            Q1=sQuery(id+"F28.wireOp",VERTEX,"E123");
            var Q2;
            Q2=sQuery(id+"F28.wireOp",VERTEX,"E124");
            var Q3;
            Q3=sQuery(id+"F28.wireOp",VERTEX,"E125");
            var Q4;
            Q4=makeQuery(id+"F29.opExtrude","SWEPT_BODY",BODY,{"disambiguationData":[OSD([sQuery(id+"F28.wireOp",EDGE,"E121.bottom"),sQuery(id+"F28.wireOp",EDGE,"E121.top"),sQuery(id+"F28.wireOp",EDGE,"E121.left"),sQuery(id+"F28.wireOp",EDGE,"E121.right"),sQuery(id+"F28.wireOp",EDGE,"E126.bottom"),sQuery(id+"F28.wireOp",EDGE,"E126.top"),sQuery(id+"F28.wireOp",EDGE,"E126.left"),sQuery(id+"F28.wireOp",EDGE,"E126.right"),sQuery(id+"F28.wireOp",EDGE,"E127.filletArc"),sQuery(id+"F28.wireOp",EDGE,"E128.filletArc"),sQuery(id+"F28.wireOp",EDGE,"E129.filletArc"),sQuery(id+"F28.wireOp",EDGE,"E130.filletArc")])]});
            hole(context, id + "F30", {"style" : HoleStyle.SIMPLE, "endStyle" : HoleEndStyle.THROUGH, "oppositeDirection" : true, "standardTappedOrClearance" : lookupTablePath({ "standard" : "ISO", "engagement" : "25%", "pitch" : "0.9 mm", "size" : "M5", "type" : "Tapped" }), "standardBlindInLast" : lookupTablePath({ "standard" : "ISO", "engagement" : "25%", "pitch" : "0.9 mm", "size" : "M5", "type" : "Tapped" }), "holeDiameter" : 4.4 * mm, "locations" : qUnion([Q0, Q1, Q2, Q3]), "scope" : qUnion([Q4]), "isTappedThrough" : true, "showTappedDepth" : true});
        }
        {
            var Q0;
            Q0=qCreatedBy(makeId("Top.planeOp"),FACE);
            var sketch = newSketch(context, id + "F31", { "sketchPlane" : qUnion([Q0])});
            skPoint(sketch, "E131", {"position": v(-184.2, -114.51) * mm});
            skPoint(sketch, "E132", {"position": v(-199.7, -99.01) * mm});
            skPoint(sketch, "E133", {"position": v(-199.7, -130.01) * mm});
            skPoint(sketch, "E134", {"position": v(-168.7, -130.01) * mm});
            skPoint(sketch, "E135", {"position": v(-168.7, -99.01) * mm});
            skPoint(sketch, "E136", {"position": v(-223.2, -85.71) * mm});
            skPoint(sketch, "E137", {"position": v(-145.2, -85.71) * mm});
            skPoint(sketch, "E138", {"position": v(-184.2, -85.71) * mm});
            skLineSegment(sketch, "E139.bottom", {"start": v(-241.2, -45.71) * mm, "end": v(-127.2, -45.71) * mm});
            skLineSegment(sketch, "E139.top", {"start": v(-241.2, -135.71) * mm, "end": v(-127.2, -135.71) * mm});
            skLineSegment(sketch, "E139.left", {"start": v(-244.2, -48.71) * mm, "end": v(-244.2, -132.71) * mm});
            skLineSegment(sketch, "E139.right", {"start": v(-124.2, -48.71) * mm, "end": v(-124.2, -132.71) * mm});
            skPoint(sketch, "E140", {"position": v(-223.2, -55.71) * mm});
            skPoint(sketch, "E141", {"position": v(-145.2, -55.71) * mm});
            skPoint(sketch, "E142", {"position": v(-233.2, -85.87) * mm});
            skPoint(sketch, "E143", {"position": v(-213.2, -85.87) * mm});
            skPoint(sketch, "E144", {"position": v(-194.2, -85.87) * mm});
            skPoint(sketch, "E145", {"position": v(-174.2, -85.87) * mm});
            skPoint(sketch, "E146", {"position": v(-155.2, -85.87) * mm});
            skPoint(sketch, "E147", {"position": v(-135.2, -85.87) * mm});
            skPoint(sketch, "E148.visualSharp", {"position": v(-244.2, -45.71) * mm});
            skArc(sketch, "E148.filletArc", {"start": v(-241.2, -45.71) * mm, "mid": v(-243.32, -46.59) * mm, "end": v(-244.2, -48.71) * mm});
            skPoint(sketch, "E149.visualSharp", {"position": v(-124.2, -45.71) * mm});
            skArc(sketch, "E149.filletArc", {"start": v(-124.2, -48.71) * mm, "mid": v(-125.08, -46.59) * mm, "end": v(-127.2, -45.71) * mm});
            skPoint(sketch, "E150.visualSharp", {"position": v(-124.2, -135.71) * mm});
            skArc(sketch, "E150.filletArc", {"start": v(-127.2, -135.71) * mm, "mid": v(-125.08, -134.83) * mm, "end": v(-124.2, -132.71) * mm});
            skPoint(sketch, "E151.visualSharp", {"position": v(-244.2, -135.71) * mm});
            skArc(sketch, "E151.filletArc", {"start": v(-244.2, -132.71) * mm, "mid": v(-243.32, -134.83) * mm, "end": v(-241.2, -135.71) * mm});
            skSolve(sketch);
        }
        {
            var Q0;
            Q0=makeQuery(id+"F31.imprint","IMPRINT",FACE,{"disambiguationData":[TD([[makeQuery(id+"F31.imprint","IMPRINT",EDGE,{"derivedFrom":sQuery(id+"F31.wireOp",EDGE,"E139.bottom")}),-1.0]])]});
            extrude(context, id + "F32", {"entities" : qUnion([Q0]), "depth" : 6 * mm});
        }
        {
            var Q0;
            Q0=sQuery(id+"F31.wireOp",VERTEX,"E132");
            var Q1;
            Q1=sQuery(id+"F31.wireOp",VERTEX,"E133");
            var Q2;
            Q2=sQuery(id+"F31.wireOp",VERTEX,"E134");
            var Q3;
            Q3=sQuery(id+"F31.wireOp",VERTEX,"E135");
            var Q4;
            Q4=sQuery(id+"F31.wireOp",VERTEX,"E142");
            var Q5;
            Q5=sQuery(id+"F31.wireOp",VERTEX,"E143");
            var Q6;
            Q6=sQuery(id+"F31.wireOp",VERTEX,"E144");
            var Q7;
            Q7=sQuery(id+"F31.wireOp",VERTEX,"E145");
            var Q8;
            Q8=sQuery(id+"F31.wireOp",VERTEX,"E146");
            var Q9;
            Q9=sQuery(id+"F31.wireOp",VERTEX,"E147");
            var Q10;
            Q10=makeQuery(id+"F32.opExtrude","SWEPT_BODY",BODY,{"disambiguationData":[OSD([sQuery(id+"F31.wireOp",EDGE,"E139.bottom"),sQuery(id+"F31.wireOp",EDGE,"E139.top"),sQuery(id+"F31.wireOp",EDGE,"E139.left"),sQuery(id+"F31.wireOp",EDGE,"E139.right"),sQuery(id+"F31.wireOp",EDGE,"E148.filletArc"),sQuery(id+"F31.wireOp",EDGE,"E149.filletArc"),sQuery(id+"F31.wireOp",EDGE,"E150.filletArc"),sQuery(id+"F31.wireOp",EDGE,"E151.filletArc")])]});
            hole(context, id + "F33", {"style" : HoleStyle.SIMPLE, "endStyle" : HoleEndStyle.THROUGH, "oppositeDirection" : true, "standardTappedOrClearance" : lookupTablePath({ "standard" : "ISO", "engagement" : "25%", "pitch" : "0.6 mm", "size" : "M3", "type" : "Tapped" }), "standardBlindInLast" : lookupTablePath({ "standard" : "ISO", "engagement" : "25%", "pitch" : "0.6 mm", "size" : "M3", "type" : "Tapped" }), "holeDiameter" : 2.6 * mm, "locations" : qUnion([Q0, Q1, Q2, Q3, Q4, Q5, Q6, Q7, Q8, Q9]), "scope" : qUnion([Q10]), "isTappedThrough" : true, "showTappedDepth" : true});
        }
        {
            var Q0;
            Q0=sQuery(id+"F31.wireOp",VERTEX,"E140");
            var Q1;
            Q1=sQuery(id+"F31.wireOp",VERTEX,"E141");
            var Q2;
            Q2=makeQuery(id+"F32.opExtrude","SWEPT_BODY",BODY,{"disambiguationData":[OSD([sQuery(id+"F31.wireOp",EDGE,"E139.bottom"),sQuery(id+"F31.wireOp",EDGE,"E139.top"),sQuery(id+"F31.wireOp",EDGE,"E139.left"),sQuery(id+"F31.wireOp",EDGE,"E139.right"),sQuery(id+"F31.wireOp",EDGE,"E148.filletArc"),sQuery(id+"F31.wireOp",EDGE,"E149.filletArc"),sQuery(id+"F31.wireOp",EDGE,"E150.filletArc"),sQuery(id+"F31.wireOp",EDGE,"E151.filletArc")])]});
            hole(context, id + "F34", {"style" : HoleStyle.SIMPLE, "endStyle" : HoleEndStyle.THROUGH, "oppositeDirection" : true, "standardTappedOrClearance" : lookupTablePath({ "standard" : "ISO", "engagement" : "25%", "pitch" : "0.9 mm", "size" : "M5", "type" : "Tapped" }), "standardBlindInLast" : lookupTablePath({ "standard" : "ISO", "engagement" : "25%", "pitch" : "0.9 mm", "size" : "M5", "type" : "Tapped" }), "holeDiameter" : 4.4 * mm, "locations" : qUnion([Q0, Q1]), "scope" : qUnion([Q2]), "isTappedThrough" : true, "showTappedDepth" : true});
        }
        {
            var Q0;
            Q0=sQuery(id+"F31.wireOp",VERTEX,"E136");
            var Q1;
            Q1=sQuery(id+"F31.wireOp",VERTEX,"E138");
            var Q2;
            Q2=sQuery(id+"F31.wireOp",VERTEX,"E137");
            var Q3;
            Q3=makeQuery(id+"F32.opExtrude","SWEPT_BODY",BODY,{"disambiguationData":[OSD([sQuery(id+"F31.wireOp",EDGE,"E139.bottom"),sQuery(id+"F31.wireOp",EDGE,"E139.top"),sQuery(id+"F31.wireOp",EDGE,"E139.left"),sQuery(id+"F31.wireOp",EDGE,"E139.right"),sQuery(id+"F31.wireOp",EDGE,"E148.filletArc"),sQuery(id+"F31.wireOp",EDGE,"E149.filletArc"),sQuery(id+"F31.wireOp",EDGE,"E150.filletArc"),sQuery(id+"F31.wireOp",EDGE,"E151.filletArc")])]});
            hole(context, id + "F35", {"style" : HoleStyle.SIMPLE, "endStyle" : HoleEndStyle.THROUGH, "oppositeDirection" : true, "standardTappedOrClearance" : lookupTablePath({ "standard" : "ISO", "size" : "8.1", "type" : "Drilled" }), "standardBlindInLast" : lookupTablePath({ "standard" : "ISO", "size" : "8.1", "type" : "Drilled" }), "holeDiameter" : 8.1 * mm, "locations" : qUnion([Q0, Q1, Q2]), "scope" : qUnion([Q3]), "isTappedThrough" : true});
        }
        {
            var Q0;
            Q0=sQuery(id+"F31.wireOp",VERTEX,"E131");
            var Q1;
            Q1=makeQuery(id+"F32.opExtrude","SWEPT_BODY",BODY,{"disambiguationData":[OSD([sQuery(id+"F31.wireOp",EDGE,"E139.bottom"),sQuery(id+"F31.wireOp",EDGE,"E139.top"),sQuery(id+"F31.wireOp",EDGE,"E139.left"),sQuery(id+"F31.wireOp",EDGE,"E139.right"),sQuery(id+"F31.wireOp",EDGE,"E148.filletArc"),sQuery(id+"F31.wireOp",EDGE,"E149.filletArc"),sQuery(id+"F31.wireOp",EDGE,"E150.filletArc"),sQuery(id+"F31.wireOp",EDGE,"E151.filletArc")])]});
            hole(context, id + "F36", {"style" : HoleStyle.SIMPLE, "endStyle" : HoleEndStyle.THROUGH, "oppositeDirection" : true, "standardTappedOrClearance" : lookupTablePath({ "standard" : "ISO", "size" : "22.5", "type" : "Drilled" }), "standardBlindInLast" : lookupTablePath({ "standard" : "ISO", "size" : "22.5", "type" : "Drilled" }), "holeDiameter" : 22.5 * mm, "locations" : qUnion([Q0]), "scope" : qUnion([Q1]), "isTappedThrough" : true});
        }
        {
            var Q0;
            Q0=qCreatedBy(makeId("Top.planeOp"),FACE);
            var sketch = newSketch(context, id + "F37", { "sketchPlane" : qUnion([Q0])});
            skArc(sketch, "E152", {"start": v(-226.53, -5.75) * mm, "mid": v(-231.53, -0.75) * mm, "end": v(-236.53, -5.75) * mm});
            skArc(sketch, "E153", {"start": v(-236.53, -25.75) * mm, "mid": v(-231.53, -30.75) * mm, "end": v(-226.53, -25.75) * mm});
            skLineSegment(sketch, "E154", {"start": v(-236.53, -5.75) * mm, "end": v(-236.53, -25.75) * mm});
            skLineSegment(sketch, "E155", {"start": v(-226.53, -5.75) * mm, "end": v(-226.53, -25.75) * mm});
            skSolve(sketch);
        }
        {
            var Q0;
            Q0=makeQuery(id+"F37.imprint","IMPRINT",FACE,{"disambiguationData":[TD([[makeQuery(id+"F37.imprint","IMPRINT",EDGE,{"derivedFrom":sQuery(id+"F37.wireOp",EDGE,"E152")}),1.0]])]});
            extrude(context, id + "F38", {"entities" : qUnion([Q0]), "depth" : 6 * mm});
        }
        {
            var Q0;
            Q0=sQuery(id+"F37.wireOp",VERTEX,"E152.center");
            var Q1;
            Q1=sQuery(id+"F37.wireOp",VERTEX,"E153.center");
            var Q2;
            Q2=makeQuery(id+"F38.opExtrude","SWEPT_BODY",BODY,{"disambiguationData":[OSD([sQuery(id+"F37.wireOp",EDGE,"E152"),sQuery(id+"F37.wireOp",EDGE,"E153"),sQuery(id+"F37.wireOp",EDGE,"E154"),sQuery(id+"F37.wireOp",EDGE,"E155")])]});
            hole(context, id + "F39", {"style" : HoleStyle.SIMPLE, "endStyle" : HoleEndStyle.THROUGH, "oppositeDirection" : true, "standardTappedOrClearance" : lookupTablePath({ "standard" : "ISO", "engagement" : "25%", "pitch" : "0.6 mm", "size" : "M3", "type" : "Tapped" }), "standardBlindInLast" : lookupTablePath({ "standard" : "ISO", "engagement" : "25%", "pitch" : "0.6 mm", "size" : "M3", "type" : "Tapped" }), "holeDiameter" : 2.6 * mm, "locations" : qUnion([Q0, Q1]), "scope" : qUnion([Q2]), "isTappedThrough" : true, "showTappedDepth" : true});
        }
        {
            var Q0;
            Q0=qCreatedBy(makeId("Top.planeOp"),FACE);
            var sketch = newSketch(context, id + "F40", { "sketchPlane" : qUnion([Q0])});
            skArc(sketch, "E156", {"start": v(-211.8, -5.62) * mm, "mid": v(-216.8, -0.62) * mm, "end": v(-221.8, -5.62) * mm});
            skArc(sketch, "E157", {"start": v(-221.8, -25.62) * mm, "mid": v(-216.8, -30.62) * mm, "end": v(-211.8, -25.62) * mm});
            skLineSegment(sketch, "E158", {"start": v(-221.8, -5.62) * mm, "end": v(-221.8, -25.62) * mm});
            skLineSegment(sketch, "E159", {"start": v(-211.8, -5.62) * mm, "end": v(-211.8, -25.62) * mm});
            skSolve(sketch);
        }
        {
            var Q0;
            Q0=makeQuery(id+"F40.imprint","IMPRINT",FACE,{"disambiguationData":[TD([[makeQuery(id+"F40.imprint","IMPRINT",EDGE,{"derivedFrom":sQuery(id+"F40.wireOp",EDGE,"E156")}),1.0]])]});
            extrude(context, id + "F41", {"entities" : qUnion([Q0]), "depth" : 6 * mm});
        }
        {
            var Q0;
            Q0=sQuery(id+"F40.wireOp",VERTEX,"E156.center");
            var Q1;
            Q1=sQuery(id+"F40.wireOp",VERTEX,"E157.center");
            var Q2;
            Q2=makeQuery(id+"F41.opExtrude","SWEPT_BODY",BODY,{"disambiguationData":[OSD([sQuery(id+"F40.wireOp",EDGE,"E156"),sQuery(id+"F40.wireOp",EDGE,"E157"),sQuery(id+"F40.wireOp",EDGE,"E158"),sQuery(id+"F40.wireOp",EDGE,"E159")])]});
            hole(context, id + "F42", {"style" : HoleStyle.SIMPLE, "endStyle" : HoleEndStyle.THROUGH, "oppositeDirection" : true, "standardTappedOrClearance" : lookupTablePath({ "standard" : "ISO", "engagement" : "25%", "pitch" : "0.6 mm", "size" : "M3", "type" : "Tapped" }), "standardBlindInLast" : lookupTablePath({ "standard" : "ISO", "engagement" : "25%", "pitch" : "0.6 mm", "size" : "M3", "type" : "Tapped" }), "holeDiameter" : 2.6 * mm, "locations" : qUnion([Q0, Q1]), "scope" : qUnion([Q2]), "isTappedThrough" : true, "showTappedDepth" : true});
        }
        {
            var Q0;
            Q0=qCreatedBy(makeId("Top.planeOp"),FACE);
            var sketch = newSketch(context, id + "F43", { "sketchPlane" : qUnion([Q0])});
            skArc(sketch, "E160", {"start": v(-197.37, -5.93) * mm, "mid": v(-202.37, -0.93) * mm, "end": v(-207.37, -5.93) * mm});
            skArc(sketch, "E161", {"start": v(-207.37, -25.93) * mm, "mid": v(-202.37, -30.93) * mm, "end": v(-197.37, -25.93) * mm});
            skLineSegment(sketch, "E162", {"start": v(-207.37, -5.93) * mm, "end": v(-207.37, -25.93) * mm});
            skLineSegment(sketch, "E163", {"start": v(-197.37, -5.93) * mm, "end": v(-197.37, -25.93) * mm});
            skSolve(sketch);
        }
        {
            var Q0;
            Q0=makeQuery(id+"F43.imprint","IMPRINT",FACE,{"disambiguationData":[TD([[makeQuery(id+"F43.imprint","IMPRINT",EDGE,{"derivedFrom":sQuery(id+"F43.wireOp",EDGE,"E160")}),1.0]])]});
            extrude(context, id + "F44", {"entities" : qUnion([Q0]), "depth" : 6 * mm});
        }
        {
            var Q0;
            Q0=sQuery(id+"F43.wireOp",VERTEX,"E160.center");
            var Q1;
            Q1=sQuery(id+"F43.wireOp",VERTEX,"E161.center");
            var Q2;
            Q2=makeQuery(id+"F44.opExtrude","SWEPT_BODY",BODY,{"disambiguationData":[OSD([sQuery(id+"F43.wireOp",EDGE,"E160"),sQuery(id+"F43.wireOp",EDGE,"E161"),sQuery(id+"F43.wireOp",EDGE,"E162"),sQuery(id+"F43.wireOp",EDGE,"E163")])]});
            hole(context, id + "F45", {"style" : HoleStyle.SIMPLE, "endStyle" : HoleEndStyle.THROUGH, "oppositeDirection" : true, "standardTappedOrClearance" : lookupTablePath({ "standard" : "ISO", "engagement" : "25%", "pitch" : "0.6 mm", "size" : "M3", "type" : "Tapped" }), "standardBlindInLast" : lookupTablePath({ "standard" : "ISO", "engagement" : "25%", "pitch" : "0.6 mm", "size" : "M3", "type" : "Tapped" }), "holeDiameter" : 2.6 * mm, "locations" : qUnion([Q0, Q1]), "scope" : qUnion([Q2]), "isTappedThrough" : true, "showTappedDepth" : true});
        }
        {
            var Q0;
            Q0=qCreatedBy(makeId("Top.planeOp"),FACE);
            var sketch = newSketch(context, id + "F46", { "sketchPlane" : qUnion([Q0])});
            skArc(sketch, "E164", {"start": v(-182.93, -7.13) * mm, "mid": v(-187.93, -2.13) * mm, "end": v(-192.93, -7.13) * mm});
            skArc(sketch, "E165", {"start": v(-192.93, -27.13) * mm, "mid": v(-187.93, -32.13) * mm, "end": v(-182.93, -27.13) * mm});
            skLineSegment(sketch, "E166", {"start": v(-192.93, -7.13) * mm, "end": v(-192.93, -27.13) * mm});
            skLineSegment(sketch, "E167", {"start": v(-182.93, -7.13) * mm, "end": v(-182.93, -27.13) * mm});
            skSolve(sketch);
        }
        {
            var Q0;
            Q0=makeQuery(id+"F46.imprint","IMPRINT",FACE,{"disambiguationData":[TD([[makeQuery(id+"F46.imprint","IMPRINT",EDGE,{"derivedFrom":sQuery(id+"F46.wireOp",EDGE,"E164")}),1.0]])]});
            extrude(context, id + "F47", {"entities" : qUnion([Q0]), "depth" : 6 * mm});
        }
        {
            var Q0;
            Q0=sQuery(id+"F46.wireOp",VERTEX,"E164.center");
            var Q1;
            Q1=sQuery(id+"F46.wireOp",VERTEX,"E165.center");
            var Q2;
            Q2=makeQuery(id+"F47.opExtrude","SWEPT_BODY",BODY,{"disambiguationData":[OSD([sQuery(id+"F46.wireOp",EDGE,"E164"),sQuery(id+"F46.wireOp",EDGE,"E165"),sQuery(id+"F46.wireOp",EDGE,"E166"),sQuery(id+"F46.wireOp",EDGE,"E167")])]});
            hole(context, id + "F48", {"style" : HoleStyle.SIMPLE, "endStyle" : HoleEndStyle.THROUGH, "oppositeDirection" : true, "standardTappedOrClearance" : lookupTablePath({ "standard" : "ISO", "engagement" : "25%", "pitch" : "0.6 mm", "size" : "M3", "type" : "Tapped" }), "standardBlindInLast" : lookupTablePath({ "standard" : "ISO", "engagement" : "25%", "pitch" : "0.6 mm", "size" : "M3", "type" : "Tapped" }), "holeDiameter" : 2.6 * mm, "locations" : qUnion([Q0, Q1]), "scope" : qUnion([Q2]), "isTappedThrough" : true, "showTappedDepth" : true});
        }
        {
            var Q0;
            Q0=qCreatedBy(makeId("Top.planeOp"),FACE);
            var sketch = newSketch(context, id + "F49", { "sketchPlane" : qUnion([Q0])});
            skArc(sketch, "E168", {"start": v(-167.41, -6.52) * mm, "mid": v(-172.41, -1.52) * mm, "end": v(-177.41, -6.52) * mm});
            skArc(sketch, "E169", {"start": v(-177.41, -26.52) * mm, "mid": v(-172.41, -31.52) * mm, "end": v(-167.41, -26.52) * mm});
            skLineSegment(sketch, "E170", {"start": v(-177.41, -6.52) * mm, "end": v(-177.41, -26.52) * mm});
            skLineSegment(sketch, "E171", {"start": v(-167.41, -6.52) * mm, "end": v(-167.41, -26.52) * mm});
            skSolve(sketch);
        }
        {
            var Q0;
            Q0=makeQuery(id+"F49.imprint","IMPRINT",FACE,{"disambiguationData":[TD([[makeQuery(id+"F49.imprint","IMPRINT",EDGE,{"derivedFrom":sQuery(id+"F49.wireOp",EDGE,"E168")}),1.0]])]});
            extrude(context, id + "F50", {"entities" : qUnion([Q0]), "depth" : 6 * mm});
        }
        {
            var Q0;
            Q0=sQuery(id+"F49.wireOp",VERTEX,"E168.center");
            var Q1;
            Q1=sQuery(id+"F49.wireOp",VERTEX,"E169.center");
            var Q2;
            Q2=makeQuery(id+"F50.opExtrude","SWEPT_BODY",BODY,{"disambiguationData":[OSD([sQuery(id+"F49.wireOp",EDGE,"E168"),sQuery(id+"F49.wireOp",EDGE,"E169"),sQuery(id+"F49.wireOp",EDGE,"E170"),sQuery(id+"F49.wireOp",EDGE,"E171")])]});
            hole(context, id + "F51", {"style" : HoleStyle.SIMPLE, "endStyle" : HoleEndStyle.THROUGH, "oppositeDirection" : true, "standardTappedOrClearance" : lookupTablePath({ "standard" : "ISO", "engagement" : "25%", "pitch" : "0.6 mm", "size" : "M3", "type" : "Tapped" }), "standardBlindInLast" : lookupTablePath({ "standard" : "ISO", "engagement" : "25%", "pitch" : "0.6 mm", "size" : "M3", "type" : "Tapped" }), "holeDiameter" : 2.6 * mm, "locations" : qUnion([Q0, Q1]), "scope" : qUnion([Q2]), "isTappedThrough" : true, "showTappedDepth" : true});
        }
        {
            var Q0;
            Q0=qCreatedBy(makeId("Top.planeOp"),FACE);
            var sketch = newSketch(context, id + "F52", { "sketchPlane" : qUnion([Q0])});
            skArc(sketch, "E172", {"start": v(-153.42, -7.02) * mm, "mid": v(-158.42, -2.02) * mm, "end": v(-163.42, -7.02) * mm});
            skArc(sketch, "E173", {"start": v(-163.42, -27.02) * mm, "mid": v(-158.42, -32.02) * mm, "end": v(-153.42, -27.02) * mm});
            skLineSegment(sketch, "E174", {"start": v(-163.42, -7.02) * mm, "end": v(-163.42, -27.02) * mm});
            skLineSegment(sketch, "E175", {"start": v(-153.42, -7.02) * mm, "end": v(-153.42, -27.02) * mm});
            skSolve(sketch);
        }
        {
            var Q0;
            Q0=makeQuery(id+"F52.imprint","IMPRINT",FACE,{"disambiguationData":[TD([[makeQuery(id+"F52.imprint","IMPRINT",EDGE,{"derivedFrom":sQuery(id+"F52.wireOp",EDGE,"E172")}),1.0]])]});
            extrude(context, id + "F53", {"entities" : qUnion([Q0]), "depth" : 6 * mm});
        }
        {
            var Q0;
            Q0=sQuery(id+"F52.wireOp",VERTEX,"E172.center");
            var Q1;
            Q1=sQuery(id+"F52.wireOp",VERTEX,"E173.center");
            var Q2;
            Q2=makeQuery(id+"F53.opExtrude","SWEPT_BODY",BODY,{"disambiguationData":[OSD([sQuery(id+"F52.wireOp",EDGE,"E172"),sQuery(id+"F52.wireOp",EDGE,"E173"),sQuery(id+"F52.wireOp",EDGE,"E174"),sQuery(id+"F52.wireOp",EDGE,"E175")])]});
            hole(context, id + "F54", {"style" : HoleStyle.SIMPLE, "endStyle" : HoleEndStyle.THROUGH, "oppositeDirection" : true, "standardTappedOrClearance" : lookupTablePath({ "standard" : "ISO", "engagement" : "25%", "pitch" : "0.6 mm", "size" : "M3", "type" : "Tapped" }), "standardBlindInLast" : lookupTablePath({ "standard" : "ISO", "engagement" : "25%", "pitch" : "0.6 mm", "size" : "M3", "type" : "Tapped" }), "holeDiameter" : 2.6 * mm, "locations" : qUnion([Q0, Q1]), "scope" : qUnion([Q2]), "isTappedThrough" : true, "showTappedDepth" : true});
        }
        {
            var Q0;
            Q0=qCreatedBy(makeId("Top.planeOp"),FACE);
            var sketch = newSketch(context, id + "F55", { "sketchPlane" : qUnion([Q0])});
            skLineSegment(sketch, "E176.bottom", {"start": v(-59.7, -95.42) * mm, "end": v(400.3, -95.42) * mm});
            skLineSegment(sketch, "E176.top", {"start": v(-59.7, -595.42) * mm, "end": v(400.3, -595.42) * mm});
            skLineSegment(sketch, "E176.left", {"start": v(-79.7, -115.42) * mm, "end": v(-79.7, -575.42) * mm});
            skLineSegment(sketch, "E176.right", {"start": v(420.3, -115.42) * mm, "end": v(420.3, -575.42) * mm});
            skLineSegment(sketch, "E177", {"start": v(-59.7, -95.42) * mm, "end": v(-59.7, -115.42) * mm});
            skLineSegment(sketch, "E178", {"start": v(-59.7, -115.42) * mm, "end": v(-79.7, -115.42) * mm});
            skLineSegment(sketch, "E179", {"start": v(400.3, -95.42) * mm, "end": v(400.3, -115.42) * mm});
            skLineSegment(sketch, "E180", {"start": v(400.3, -115.42) * mm, "end": v(420.3, -115.42) * mm});
            skLineSegment(sketch, "E181", {"start": v(420.3, -575.42) * mm, "end": v(400.3, -575.42) * mm});
            skLineSegment(sketch, "E182", {"start": v(400.3, -575.42) * mm, "end": v(400.3, -595.42) * mm});
            skLineSegment(sketch, "E183", {"start": v(-79.7, -575.42) * mm, "end": v(-59.7, -575.42) * mm});
            skLineSegment(sketch, "E184", {"start": v(-59.7, -575.42) * mm, "end": v(-59.7, -595.42) * mm});
            skPoint(sketch, "E185", {"position": v(90.3, -105.42) * mm});
            skPoint(sketch, "E186", {"position": v(250.3, -105.42) * mm});
            skPoint(sketch, "E187", {"position": v(410.3, -265.42) * mm});
            skPoint(sketch, "E188", {"position": v(410.3, -425.42) * mm});
            skPoint(sketch, "E189", {"position": v(250.3, -585.42) * mm});
            skPoint(sketch, "E190", {"position": v(90.3, -585.42) * mm});
            skPoint(sketch, "E191", {"position": v(-69.7, -265.42) * mm});
            skPoint(sketch, "E192", {"position": v(-69.7, -425.42) * mm});
            skPoint(sketch, "E193", {"position": v(180.3, -164.22) * mm});
            skPoint(sketch, "E194", {"position": v(141.3, -135.42) * mm});
            skPoint(sketch, "E195", {"position": v(219.3, -135.42) * mm});
            skPoint(sketch, "E196", {"position": v(180.3, -135.42) * mm});
            skPoint(sketch, "E197", {"position": v(131.3, -135.42) * mm});
            skPoint(sketch, "E198", {"position": v(151.3, -135.42) * mm});
            skPoint(sketch, "E199", {"position": v(170.3, -135.42) * mm});
            skPoint(sketch, "E200", {"position": v(190.3, -135.42) * mm});
            skPoint(sketch, "E201", {"position": v(209.3, -135.42) * mm});
            skPoint(sketch, "E202", {"position": v(229.3, -135.42) * mm});
            skPoint(sketch, "E203", {"position": v(162.3, -164.22) * mm});
            skPoint(sketch, "E204", {"position": v(198.3, -164.22) * mm});
            skSolve(sketch);
        }
        {
            var Q0;
            Q0=makeQuery(id+"F55.imprint","IMPRINT",FACE,{"disambiguationData":[TD([[makeQuery(id+"F55.imprint","IMPRINT",EDGE,{"derivedFrom":sQuery(id+"F55.wireOp",EDGE,"E176.bottom")}),-1.0]])]});
            extrude(context, id + "F56", {"entities" : qUnion([Q0]), "depth" : 6 * mm});
        }
        {
            var Q0;
            Q0=sQuery(id+"F55.wireOp",VERTEX,"E185");
            var Q1;
            Q1=sQuery(id+"F55.wireOp",VERTEX,"E186");
            var Q2;
            Q2=sQuery(id+"F55.wireOp",VERTEX,"E191");
            var Q3;
            Q3=sQuery(id+"F55.wireOp",VERTEX,"E192");
            var Q4;
            Q4=sQuery(id+"F55.wireOp",VERTEX,"E187");
            var Q5;
            Q5=sQuery(id+"F55.wireOp",VERTEX,"E188");
            var Q6;
            Q6=sQuery(id+"F55.wireOp",VERTEX,"E189");
            var Q7;
            Q7=sQuery(id+"F55.wireOp",VERTEX,"E190");
            var Q8;
            Q8=sQuery(id+"F55.wireOp",VERTEX,"E203");
            var Q9;
            Q9=sQuery(id+"F55.wireOp",VERTEX,"E204");
            var Q10;
            Q10=makeQuery(id+"F56.opExtrude","SWEPT_BODY",BODY,{"disambiguationData":[OSD([sQuery(id+"F55.wireOp",EDGE,"E176.bottom"),sQuery(id+"F55.wireOp",EDGE,"E176.top"),sQuery(id+"F55.wireOp",EDGE,"E176.left"),sQuery(id+"F55.wireOp",EDGE,"E176.right"),sQuery(id+"F55.wireOp",EDGE,"E177"),sQuery(id+"F55.wireOp",EDGE,"E178"),sQuery(id+"F55.wireOp",EDGE,"E179"),sQuery(id+"F55.wireOp",EDGE,"E180"),sQuery(id+"F55.wireOp",EDGE,"E181"),sQuery(id+"F55.wireOp",EDGE,"E182"),sQuery(id+"F55.wireOp",EDGE,"E183"),sQuery(id+"F55.wireOp",EDGE,"E184")])]});
            hole(context, id + "F57", {"style" : HoleStyle.SIMPLE, "endStyle" : HoleEndStyle.THROUGH, "oppositeDirection" : true, "standardTappedOrClearance" : lookupTablePath({ "standard" : "ISO", "engagement" : "25%", "pitch" : "0.9 mm", "size" : "M5", "type" : "Tapped" }), "standardBlindInLast" : lookupTablePath({ "standard" : "ISO", "engagement" : "25%", "pitch" : "0.9 mm", "size" : "M5", "type" : "Tapped" }), "holeDiameter" : 4.4 * mm, "locations" : qUnion([Q0, Q1, Q2, Q3, Q4, Q5, Q6, Q7, Q8, Q9]), "scope" : qUnion([Q10]), "isTappedThrough" : true, "showTappedDepth" : true});
        }
        {
            var Q0;
            Q0=sQuery(id+"F55.wireOp",VERTEX,"E197");
            var Q1;
            Q1=sQuery(id+"F55.wireOp",VERTEX,"E198");
            var Q2;
            Q2=sQuery(id+"F55.wireOp",VERTEX,"E199");
            var Q3;
            Q3=sQuery(id+"F55.wireOp",VERTEX,"E200");
            var Q4;
            Q4=sQuery(id+"F55.wireOp",VERTEX,"E201");
            var Q5;
            Q5=sQuery(id+"F55.wireOp",VERTEX,"E202");
            var Q6;
            Q6=makeQuery(id+"F56.opExtrude","SWEPT_BODY",BODY,{"disambiguationData":[OSD([sQuery(id+"F55.wireOp",EDGE,"E176.bottom"),sQuery(id+"F55.wireOp",EDGE,"E176.top"),sQuery(id+"F55.wireOp",EDGE,"E176.left"),sQuery(id+"F55.wireOp",EDGE,"E176.right"),sQuery(id+"F55.wireOp",EDGE,"E177"),sQuery(id+"F55.wireOp",EDGE,"E178"),sQuery(id+"F55.wireOp",EDGE,"E179"),sQuery(id+"F55.wireOp",EDGE,"E180"),sQuery(id+"F55.wireOp",EDGE,"E181"),sQuery(id+"F55.wireOp",EDGE,"E182"),sQuery(id+"F55.wireOp",EDGE,"E183"),sQuery(id+"F55.wireOp",EDGE,"E184")])]});
            hole(context, id + "F58", {"style" : HoleStyle.SIMPLE, "endStyle" : HoleEndStyle.THROUGH, "oppositeDirection" : true, "standardTappedOrClearance" : lookupTablePath({ "standard" : "ISO", "engagement" : "25%", "pitch" : "0.6 mm", "size" : "M3", "type" : "Tapped" }), "standardBlindInLast" : lookupTablePath({ "standard" : "ISO", "engagement" : "25%", "pitch" : "0.6 mm", "size" : "M3", "type" : "Tapped" }), "holeDiameter" : 2.6 * mm, "locations" : qUnion([Q0, Q1, Q2, Q3, Q4, Q5]), "scope" : qUnion([Q6]), "isTappedThrough" : true, "showTappedDepth" : true});
        }
        {
            var Q0;
            Q0=sQuery(id+"F55.wireOp",VERTEX,"E194");
            var Q1;
            Q1=sQuery(id+"F55.wireOp",VERTEX,"E196");
            var Q2;
            Q2=sQuery(id+"F55.wireOp",VERTEX,"E195");
            var Q3;
            Q3=makeQuery(id+"F56.opExtrude","SWEPT_BODY",BODY,{"disambiguationData":[OSD([sQuery(id+"F55.wireOp",EDGE,"E176.bottom"),sQuery(id+"F55.wireOp",EDGE,"E176.top"),sQuery(id+"F55.wireOp",EDGE,"E176.left"),sQuery(id+"F55.wireOp",EDGE,"E176.right"),sQuery(id+"F55.wireOp",EDGE,"E177"),sQuery(id+"F55.wireOp",EDGE,"E178"),sQuery(id+"F55.wireOp",EDGE,"E179"),sQuery(id+"F55.wireOp",EDGE,"E180"),sQuery(id+"F55.wireOp",EDGE,"E181"),sQuery(id+"F55.wireOp",EDGE,"E182"),sQuery(id+"F55.wireOp",EDGE,"E183"),sQuery(id+"F55.wireOp",EDGE,"E184")])]});
            hole(context, id + "F59", {"style" : HoleStyle.SIMPLE, "endStyle" : HoleEndStyle.THROUGH, "oppositeDirection" : true, "standardTappedOrClearance" : lookupTablePath({ "standard" : "ISO", "size" : "8.1", "type" : "Drilled" }), "standardBlindInLast" : lookupTablePath({ "standard" : "ISO", "size" : "8.1", "type" : "Drilled" }), "holeDiameter" : 8.1 * mm, "locations" : qUnion([Q0, Q1, Q2]), "scope" : qUnion([Q3]), "isTappedThrough" : true});
        }
        {
            var Q0;
            Q0=sQuery(id+"F55.wireOp",VERTEX,"E193");
            var Q1;
            Q1=makeQuery(id+"F56.opExtrude","SWEPT_BODY",BODY,{"disambiguationData":[OSD([sQuery(id+"F55.wireOp",EDGE,"E176.bottom"),sQuery(id+"F55.wireOp",EDGE,"E176.top"),sQuery(id+"F55.wireOp",EDGE,"E176.left"),sQuery(id+"F55.wireOp",EDGE,"E176.right"),sQuery(id+"F55.wireOp",EDGE,"E177"),sQuery(id+"F55.wireOp",EDGE,"E178"),sQuery(id+"F55.wireOp",EDGE,"E179"),sQuery(id+"F55.wireOp",EDGE,"E180"),sQuery(id+"F55.wireOp",EDGE,"E181"),sQuery(id+"F55.wireOp",EDGE,"E182"),sQuery(id+"F55.wireOp",EDGE,"E183"),sQuery(id+"F55.wireOp",EDGE,"E184")])]});
            hole(context, id + "F60", {"style" : HoleStyle.SIMPLE, "endStyle" : HoleEndStyle.THROUGH, "oppositeDirection" : true, "standardTappedOrClearance" : lookupTablePath({ "standard" : "ISO", "size" : "8.4", "type" : "Drilled" }), "standardBlindInLast" : lookupTablePath({ "standard" : "ISO", "size" : "8.4", "type" : "Drilled" }), "holeDiameter" : 8.4 * mm, "locations" : qUnion([Q0]), "scope" : qUnion([Q1]), "isTappedThrough" : true});
        }
        {
            var Q0;
            Q0=makeQuery(id+"F3.opExtrude","SWEPT_BODY",BODY,{"disambiguationData":[OSD([sQuery(id+"F2.wireOp",EDGE,"E22.bottom"),sQuery(id+"F2.wireOp",EDGE,"E22.top"),sQuery(id+"F2.wireOp",EDGE,"E22.left"),sQuery(id+"F2.wireOp",EDGE,"E22.right"),sQuery(id+"F2.wireOp",EDGE,"E23"),sQuery(id+"F2.wireOp",EDGE,"E24"),sQuery(id+"F2.wireOp",EDGE,"E25"),sQuery(id+"F2.wireOp",EDGE,"E26"),sQuery(id+"F2.wireOp",EDGE,"E27"),sQuery(id+"F2.wireOp",EDGE,"E28"),sQuery(id+"F2.wireOp",EDGE,"E29"),sQuery(id+"F2.wireOp",EDGE,"E30"),sQuery(id+"F2.wireOp",EDGE,"E31.bottom"),sQuery(id+"F2.wireOp",EDGE,"E31.top"),sQuery(id+"F2.wireOp",EDGE,"E31.left"),sQuery(id+"F2.wireOp",EDGE,"E31.right"),sQuery(id+"F2.wireOp",EDGE,"E32.bottom"),sQuery(id+"F2.wireOp",EDGE,"E32.top"),sQuery(id+"F2.wireOp",EDGE,"E32.left"),sQuery(id+"F2.wireOp",EDGE,"E32.right"),sQuery(id+"F2.wireOp",EDGE,"E33.filletArc"),sQuery(id+"F2.wireOp",EDGE,"E34.filletArc"),sQuery(id+"F2.wireOp",EDGE,"E35.filletArc"),sQuery(id+"F2.wireOp",EDGE,"E36.filletArc"),sQuery(id+"F2.wireOp",EDGE,"E37")])]});
            var Q1;
            Q1=makeQuery(id+"F3.opExtrude","CAP_FACE",FACE,{"disambiguationData":[OSD([sQuery(id+"F2.wireOp",EDGE,"E22.bottom"),sQuery(id+"F2.wireOp",EDGE,"E22.top"),sQuery(id+"F2.wireOp",EDGE,"E22.left"),sQuery(id+"F2.wireOp",EDGE,"E22.right"),sQuery(id+"F2.wireOp",EDGE,"E23"),sQuery(id+"F2.wireOp",EDGE,"E24"),sQuery(id+"F2.wireOp",EDGE,"E25"),sQuery(id+"F2.wireOp",EDGE,"E26"),sQuery(id+"F2.wireOp",EDGE,"E27"),sQuery(id+"F2.wireOp",EDGE,"E28"),sQuery(id+"F2.wireOp",EDGE,"E29"),sQuery(id+"F2.wireOp",EDGE,"E30"),sQuery(id+"F2.wireOp",EDGE,"E31.bottom"),sQuery(id+"F2.wireOp",EDGE,"E31.top"),sQuery(id+"F2.wireOp",EDGE,"E31.left"),sQuery(id+"F2.wireOp",EDGE,"E31.right"),sQuery(id+"F2.wireOp",EDGE,"E32.bottom"),sQuery(id+"F2.wireOp",EDGE,"E32.top"),sQuery(id+"F2.wireOp",EDGE,"E32.left"),sQuery(id+"F2.wireOp",EDGE,"E32.right"),sQuery(id+"F2.wireOp",EDGE,"E33.filletArc"),sQuery(id+"F2.wireOp",EDGE,"E34.filletArc"),sQuery(id+"F2.wireOp",EDGE,"E35.filletArc"),sQuery(id+"F2.wireOp",EDGE,"E36.filletArc"),sQuery(id+"F2.wireOp",EDGE,"E37")])],"isStart":false});
            transform(context, id + "F61", {"entities" : qUnion([Q0]), "transformType" : TransformType.TRANSLATION_3D, "dx" : -288 * mm, "dy" : -251 * mm, "dz" : 0 * mm, "makeCopy" : false});
        }
        {
            var Q0;
            Q0=makeQuery(id+"F5.opExtrude","SWEPT_BODY",BODY,{"disambiguationData":[OSD([sQuery(id+"F4.wireOp",EDGE,"E38.bottom"),sQuery(id+"F4.wireOp",EDGE,"E38.top"),sQuery(id+"F4.wireOp",EDGE,"E38.left"),sQuery(id+"F4.wireOp",EDGE,"E38.right"),sQuery(id+"F4.wireOp",EDGE,"E39"),sQuery(id+"F4.wireOp",EDGE,"E40"),sQuery(id+"F4.wireOp",EDGE,"E41"),sQuery(id+"F4.wireOp",EDGE,"E42"),sQuery(id+"F4.wireOp",EDGE,"E43"),sQuery(id+"F4.wireOp",EDGE,"E44"),sQuery(id+"F4.wireOp",EDGE,"E45"),sQuery(id+"F4.wireOp",EDGE,"E46"),sQuery(id+"F4.wireOp",EDGE,"E47"),sQuery(id+"F4.wireOp",EDGE,"E48"),sQuery(id+"F4.wireOp",EDGE,"E49.bottom"),sQuery(id+"F4.wireOp",EDGE,"E49.top"),sQuery(id+"F4.wireOp",EDGE,"E49.left"),sQuery(id+"F4.wireOp",EDGE,"E49.right"),sQuery(id+"F4.wireOp",EDGE,"E50.filletArc"),sQuery(id+"F4.wireOp",EDGE,"E51.filletArc"),sQuery(id+"F4.wireOp",EDGE,"E52.filletArc"),sQuery(id+"F4.wireOp",EDGE,"E53.filletArc"),sQuery(id+"F4.wireOp",EDGE,"E54.filletArc"),sQuery(id+"F4.wireOp",EDGE,"E55.filletArc"),sQuery(id+"F4.wireOp",EDGE,"E56.filletArc"),sQuery(id+"F4.wireOp",EDGE,"E57.filletArc"),sQuery(id+"F4.wireOp",EDGE,"E58"),sQuery(id+"F4.wireOp",EDGE,"E59"),sQuery(id+"F4.wireOp",EDGE,"1IpveIvp-qXlS-DRw4-WFvo-TBxESb9HgY2E"),sQuery(id+"F4.wireOp",EDGE,"sxBF0yuj-ktqb-lqD6-N3Hc-lJfuUTqGLgTc"),sQuery(id+"F4.wireOp",EDGE,"5rScdfc3-lKWb-BmLE-7BWn-HCKHA5jRaWxi"),sQuery(id+"F4.wireOp",EDGE,"E60.trimOffspring"),sQuery(id+"F4.wireOp",EDGE,"db613344-cd4a-4a6c-b34d-b9b231ac8cee.filletArc"),sQuery(id+"F4.wireOp",EDGE,"f34d9bfb-f96e-47b5-92aa-bb080836b140.filletArc")])]});
            transform(context, id + "F62", {"entities" : qUnion([Q0]), "transformType" : TransformType.TRANSLATION_3D, "dx" : -198 * mm, "dy" : -262 * mm, "dz" : 0 * mm, "makeCopy" : false});
        }
        {
            var Q0;
            Q0=makeQuery(id+"F56.opExtrude","SWEPT_BODY",BODY,{"disambiguationData":[OSD([sQuery(id+"F55.wireOp",EDGE,"E176.bottom"),sQuery(id+"F55.wireOp",EDGE,"E176.top"),sQuery(id+"F55.wireOp",EDGE,"E176.left"),sQuery(id+"F55.wireOp",EDGE,"E176.right"),sQuery(id+"F55.wireOp",EDGE,"E177"),sQuery(id+"F55.wireOp",EDGE,"E178"),sQuery(id+"F55.wireOp",EDGE,"E179"),sQuery(id+"F55.wireOp",EDGE,"E180"),sQuery(id+"F55.wireOp",EDGE,"E181"),sQuery(id+"F55.wireOp",EDGE,"E182"),sQuery(id+"F55.wireOp",EDGE,"E183"),sQuery(id+"F55.wireOp",EDGE,"E184")])]});
            transform(context, id + "F63", {"entities" : qUnion([Q0]), "transformType" : TransformType.TRANSLATION_3D, "dx" : 155 * mm, "dy" : 0 * mm, "dz" : 0 * mm, "makeCopy" : false});
        }
        {
            var Q0;
            Q0=makeQuery(id+"F11.opExtrude","SWEPT_BODY",BODY,{"disambiguationData":[OSD([sQuery(id+"F10.wireOp",EDGE,"E92.bottom"),sQuery(id+"F10.wireOp",EDGE,"E92.top"),sQuery(id+"F10.wireOp",EDGE,"E92.left"),sQuery(id+"F10.wireOp",EDGE,"E92.right"),sQuery(id+"F10.wireOp",EDGE,"E93.filletArc"),sQuery(id+"F10.wireOp",EDGE,"E94.filletArc"),sQuery(id+"F10.wireOp",EDGE,"E95.filletArc"),sQuery(id+"F10.wireOp",EDGE,"E96.filletArc")])]});
            var Q1;
            Q1=makeQuery(id+"F14.opExtrude","SWEPT_BODY",BODY,{"disambiguationData":[OSD([sQuery(id+"F13.wireOp",EDGE,"E100.bottom"),sQuery(id+"F13.wireOp",EDGE,"E100.top"),sQuery(id+"F13.wireOp",EDGE,"E100.left"),sQuery(id+"F13.wireOp",EDGE,"E100.right"),sQuery(id+"F13.wireOp",EDGE,"E101.filletArc"),sQuery(id+"F13.wireOp",EDGE,"E102.filletArc"),sQuery(id+"F13.wireOp",EDGE,"E103.filletArc"),sQuery(id+"F13.wireOp",EDGE,"E104.filletArc")])]});
            var Q2;
            Q2=makeQuery(id+"F17.opExtrude","SWEPT_BODY",BODY,{"disambiguationData":[OSD([sQuery(id+"F16.wireOp",EDGE,"E108")])]});
            var Q3;
            Q3=makeQuery(id+"F20.opExtrude","SWEPT_BODY",BODY,{"disambiguationData":[OSD([sQuery(id+"F19.wireOp",EDGE,"E109")])]});
            var Q4;
            Q4=makeQuery(id+"F23.opExtrude","SWEPT_BODY",BODY,{"disambiguationData":[OSD([sQuery(id+"F22.wireOp",EDGE,"E110")])]});
            var Q5;
            Q5=makeQuery(id+"F26.opExtrude","SWEPT_BODY",BODY,{"disambiguationData":[OSD([sQuery(id+"F25.wireOp",EDGE,"E111.bottom"),sQuery(id+"F25.wireOp",EDGE,"E111.top"),sQuery(id+"F25.wireOp",EDGE,"E111.left"),sQuery(id+"F25.wireOp",EDGE,"E111.right"),sQuery(id+"F25.wireOp",EDGE,"E116.bottom"),sQuery(id+"F25.wireOp",EDGE,"E116.top"),sQuery(id+"F25.wireOp",EDGE,"E116.left"),sQuery(id+"F25.wireOp",EDGE,"E116.right"),sQuery(id+"F25.wireOp",EDGE,"E117.filletArc"),sQuery(id+"F25.wireOp",EDGE,"E118.filletArc"),sQuery(id+"F25.wireOp",EDGE,"E119.filletArc"),sQuery(id+"F25.wireOp",EDGE,"E120.filletArc")])]});
            var Q6;
            Q6=makeQuery(id+"F29.opExtrude","SWEPT_BODY",BODY,{"disambiguationData":[OSD([sQuery(id+"F28.wireOp",EDGE,"E121.bottom"),sQuery(id+"F28.wireOp",EDGE,"E121.top"),sQuery(id+"F28.wireOp",EDGE,"E121.left"),sQuery(id+"F28.wireOp",EDGE,"E121.right"),sQuery(id+"F28.wireOp",EDGE,"E126.bottom"),sQuery(id+"F28.wireOp",EDGE,"E126.top"),sQuery(id+"F28.wireOp",EDGE,"E126.left"),sQuery(id+"F28.wireOp",EDGE,"E126.right"),sQuery(id+"F28.wireOp",EDGE,"E127.filletArc"),sQuery(id+"F28.wireOp",EDGE,"E128.filletArc"),sQuery(id+"F28.wireOp",EDGE,"E129.filletArc"),sQuery(id+"F28.wireOp",EDGE,"E130.filletArc")])]});
            transform(context, id + "F64", {"entities" : qUnion([Q0, Q1, Q2, Q3, Q4, Q5, Q6]), "transformType" : TransformType.TRANSLATION_3D, "dx" : -130 * mm, "dy" : -161 * mm, "dz" : 0 * mm, "makeCopy" : false});
        }
        {
            var Q0;
            Q0=makeQuery(id+"F32.opExtrude","SWEPT_BODY",BODY,{"disambiguationData":[OSD([sQuery(id+"F31.wireOp",EDGE,"E139.bottom"),sQuery(id+"F31.wireOp",EDGE,"E139.top"),sQuery(id+"F31.wireOp",EDGE,"E139.left"),sQuery(id+"F31.wireOp",EDGE,"E139.right"),sQuery(id+"F31.wireOp",EDGE,"E148.filletArc"),sQuery(id+"F31.wireOp",EDGE,"E149.filletArc"),sQuery(id+"F31.wireOp",EDGE,"E150.filletArc"),sQuery(id+"F31.wireOp",EDGE,"E151.filletArc")])]});
            transform(context, id + "F65", {"entities" : qUnion([Q0]), "transformType" : TransformType.TRANSLATION_3D, "dx" : 11 * mm, "dy" : 0 * mm, "dz" : 0 * mm, "makeCopy" : false});
        }
        {
            var Q0;
            Q0=makeQuery(id+"F56.opExtrude","SWEPT_BODY",BODY,{"disambiguationData":[OSD([sQuery(id+"F55.wireOp",EDGE,"E176.bottom"),sQuery(id+"F55.wireOp",EDGE,"E176.top"),sQuery(id+"F55.wireOp",EDGE,"E176.left"),sQuery(id+"F55.wireOp",EDGE,"E176.right"),sQuery(id+"F55.wireOp",EDGE,"E177"),sQuery(id+"F55.wireOp",EDGE,"E178"),sQuery(id+"F55.wireOp",EDGE,"E179"),sQuery(id+"F55.wireOp",EDGE,"E180"),sQuery(id+"F55.wireOp",EDGE,"E181"),sQuery(id+"F55.wireOp",EDGE,"E182"),sQuery(id+"F55.wireOp",EDGE,"E183"),sQuery(id+"F55.wireOp",EDGE,"E184")])]});
            transform(context, id + "F66", {"entities" : qUnion([Q0]), "transformType" : TransformType.TRANSLATION_3D, "dx" : -94 * mm, "dy" : 331 * mm, "dz" : 0 * mm, "makeCopy" : false});
        }
        {
            var Q0;
            Q0=qCreatedBy(makeId("Top.planeOp"),FACE);
            var sketch = newSketch(context, id + "F67", { "sketchPlane" : qUnion([Q0])});
            skLineSegment(sketch, "E205.bottom", {"start": v(-133.13, -2.75) * mm, "end": v(-117.13, -2.75) * mm});
            skLineSegment(sketch, "E205.top", {"start": v(-133.13, -14.75) * mm, "end": v(-117.13, -14.75) * mm});
            skLineSegment(sketch, "E205.left", {"start": v(-133.13, -2.75) * mm, "end": v(-133.13, -14.75) * mm});
            skLineSegment(sketch, "E205.right", {"start": v(-117.13, -2.75) * mm, "end": v(-117.13, -14.75) * mm});
            skPoint(sketch, "E206", {"position": v(-129.38, -8.75) * mm});
            skPoint(sketch, "E207", {"position": v(-120.88, -8.75) * mm});
            skSolve(sketch);
        }
        {
            var Q0;
            Q0=makeQuery(id+"F67.imprint","IMPRINT",FACE,{"disambiguationData":[TD([[makeQuery(id+"F67.imprint","IMPRINT",EDGE,{"derivedFrom":sQuery(id+"F67.wireOp",EDGE,"E205.bottom")}),-1.0]])]});
            extrude(context, id + "F68", {"entities" : qUnion([Q0]), "depth" : 6 * mm});
        }
        {
            var Q0;
            Q0=sQuery(id+"F67.wireOp",VERTEX,"E206");
            var Q1;
            Q1=sQuery(id+"F67.wireOp",VERTEX,"E207");
            var Q2;
            Q2=makeQuery(id+"F68.opExtrude","SWEPT_BODY",BODY,{"disambiguationData":[OSD([sQuery(id+"F67.wireOp",EDGE,"E205.bottom"),sQuery(id+"F67.wireOp",EDGE,"E205.top"),sQuery(id+"F67.wireOp",EDGE,"E205.left"),sQuery(id+"F67.wireOp",EDGE,"E205.right")])]});
            hole(context, id + "F69", {"style" : HoleStyle.SIMPLE, "endStyle" : HoleEndStyle.THROUGH, "oppositeDirection" : true, "standardTappedOrClearance" : lookupTablePath({ "standard" : "ISO", "engagement" : "25%", "pitch" : "0.6 mm", "size" : "M3", "type" : "Tapped" }), "standardBlindInLast" : lookupTablePath({ "standard" : "ISO", "engagement" : "25%", "pitch" : "0.6 mm", "size" : "M3", "type" : "Tapped" }), "holeDiameter" : 2.6 * mm, "locations" : qUnion([Q0, Q1]), "scope" : qUnion([Q2]), "isTappedThrough" : true, "showTappedDepth" : true});
        }
        {
            var Q0;
            Q0=qCreatedBy(makeId("Top.planeOp"),FACE);
            var sketch = newSketch(context, id + "F70", { "sketchPlane" : qUnion([Q0])});
            skLineSegment(sketch, "E208.bottom", {"start": v(-112.75, 200.06) * mm, "end": v(-69.25, 200.06) * mm});
            skLineSegment(sketch, "E208.top", {"start": v(-112.75, 145.06) * mm, "end": v(-69.25, 145.06) * mm});
            skLineSegment(sketch, "E208.left", {"start": v(-115.75, 197.06) * mm, "end": v(-115.75, 148.06) * mm});
            skLineSegment(sketch, "E208.right", {"start": v(-66.25, 197.06) * mm, "end": v(-66.25, 148.06) * mm});
            skPoint(sketch, "E209", {"position": v(-91, 182.56) * mm});
            skPoint(sketch, "E210", {"position": v(-75, 182.56) * mm});
            skPoint(sketch, "E211", {"position": v(-107, 182.56) * mm});
            skPoint(sketch, "E212.visualSharp", {"position": v(-115.75, 200.06) * mm});
            skArc(sketch, "E212.filletArc", {"start": v(-112.75, 200.06) * mm, "mid": v(-114.87, 199.18) * mm, "end": v(-115.75, 197.06) * mm});
            skPoint(sketch, "E213.visualSharp", {"position": v(-66.25, 200.06) * mm});
            skArc(sketch, "E213.filletArc", {"start": v(-66.25, 197.06) * mm, "mid": v(-67.12, 199.18) * mm, "end": v(-69.25, 200.06) * mm});
            skPoint(sketch, "E214.visualSharp", {"position": v(-66.25, 145.06) * mm});
            skArc(sketch, "E214.filletArc", {"start": v(-69.25, 145.06) * mm, "mid": v(-67.12, 145.93) * mm, "end": v(-66.25, 148.06) * mm});
            skPoint(sketch, "E215.visualSharp", {"position": v(-115.75, 145.06) * mm});
            skArc(sketch, "E215.filletArc", {"start": v(-115.75, 148.06) * mm, "mid": v(-114.87, 145.93) * mm, "end": v(-112.75, 145.06) * mm});
            skSolve(sketch);
        }
        {
            var Q0;
            Q0=makeQuery(id+"F70.imprint","IMPRINT",FACE,{"disambiguationData":[TD([[makeQuery(id+"F70.imprint","IMPRINT",EDGE,{"derivedFrom":sQuery(id+"F70.wireOp",EDGE,"E208.bottom")}),-1.0]])]});
            extrude(context, id + "F71", {"entities" : qUnion([Q0]), "depth" : 6 * mm});
        }
        {
            var Q0;
            Q0=sQuery(id+"F70.wireOp",VERTEX,"E211");
            var Q1;
            Q1=sQuery(id+"F70.wireOp",VERTEX,"E210");
            var Q2;
            Q2=makeQuery(id+"F71.opExtrude","SWEPT_BODY",BODY,{"disambiguationData":[OSD([sQuery(id+"F70.wireOp",EDGE,"E208.bottom"),sQuery(id+"F70.wireOp",EDGE,"E208.top"),sQuery(id+"F70.wireOp",EDGE,"E208.left"),sQuery(id+"F70.wireOp",EDGE,"E208.right")])]});
            hole(context, id + "F72", {"style" : HoleStyle.SIMPLE, "endStyle" : HoleEndStyle.THROUGH, "oppositeDirection" : true, "standardTappedOrClearance" : lookupTablePath({ "standard" : "ISO", "engagement" : "25%", "pitch" : "0.75 mm", "size" : "M4", "type" : "Tapped" }), "standardBlindInLast" : lookupTablePath({ "standard" : "ISO", "engagement" : "25%", "pitch" : "0.75 mm", "size" : "M4", "type" : "Tapped" }), "holeDiameter" : 3.5 * mm, "locations" : qUnion([Q0, Q1]), "scope" : qUnion([Q2]), "isTappedThrough" : true, "showTappedDepth" : true});
        }
        {
            var Q0;
            Q0=sQuery(id+"F70.wireOp",VERTEX,"E209");
            var Q1;
            Q1=makeQuery(id+"F71.opExtrude","SWEPT_BODY",BODY,{"disambiguationData":[OSD([sQuery(id+"F70.wireOp",EDGE,"E208.bottom"),sQuery(id+"F70.wireOp",EDGE,"E208.top"),sQuery(id+"F70.wireOp",EDGE,"E208.left"),sQuery(id+"F70.wireOp",EDGE,"E208.right")])]});
            hole(context, id + "F73", {"style" : HoleStyle.SIMPLE, "endStyle" : HoleEndStyle.THROUGH, "oppositeDirection" : true, "standardTappedOrClearance" : lookupTablePath({ "standard" : "ISO", "size" : "22.5", "type" : "Drilled" }), "standardBlindInLast" : lookupTablePath({ "standard" : "ISO", "size" : "22.5", "type" : "Drilled" }), "holeDiameter" : 22.5 * mm, "locations" : qUnion([Q0]), "scope" : qUnion([Q1]), "isTappedThrough" : true});
        }
        {
            var Q0;
            Q0=qCreatedBy(makeId("Top.planeOp"),FACE);
            var sketch = newSketch(context, id + "F74", { "sketchPlane" : qUnion([Q0])});
            skArc(sketch, "E216", {"start": v(-97.85, 136.55) * mm, "mid": v(-100.14, 136.03) * mm, "end": v(-101.97, 134.55) * mm});
            skArc(sketch, "E217", {"start": v(-86.25, 126.05) * mm, "mid": v(-83.96, 126.58) * mm, "end": v(-82.13, 128.05) * mm});
            skLineSegment(sketch, "E218.bottom", {"start": v(-113.05, 134.55) * mm, "end": v(-101.97, 134.55) * mm});
            skLineSegment(sketch, "E218.top", {"start": v(-113.05, 128.05) * mm, "end": v(-101.97, 128.05) * mm});
            skLineSegment(sketch, "E218.left", {"start": v(-113.05, 134.55) * mm, "end": v(-113.05, 128.05) * mm});
            skLineSegment(sketch, "E218.right", {"start": v(-71.05, 134.55) * mm, "end": v(-71.05, 128.05) * mm});
            skLineSegment(sketch, "E219", {"start": v(-97.85, 136.55) * mm, "end": v(-86.25, 136.55) * mm});
            skLineSegment(sketch, "E220", {"start": v(-97.85, 126.05) * mm, "end": v(-86.25, 126.05) * mm});
            skLineSegment(sketch, "E221.trimOffspring", {"start": v(-82.13, 134.55) * mm, "end": v(-71.05, 134.55) * mm});
            skLineSegment(sketch, "E222.trimOffspring", {"start": v(-82.13, 128.05) * mm, "end": v(-71.05, 128.05) * mm});
            skArc(sketch, "E223.trimOffspring", {"start": v(-101.97, 128.05) * mm, "mid": v(-100.14, 126.58) * mm, "end": v(-97.85, 126.05) * mm});
            skArc(sketch, "E224.trimOffspring", {"start": v(-82.13, 134.55) * mm, "mid": v(-83.96, 136.03) * mm, "end": v(-86.25, 136.55) * mm});
            skSolve(sketch);
        }
        {
            var Q0;
            Q0=makeQuery(id+"F74.imprint","IMPRINT",FACE,{"disambiguationData":[TD([[makeQuery(id+"F74.imprint","IMPRINT",EDGE,{"derivedFrom":sQuery(id+"F74.wireOp",EDGE,"E216")}),1.0]])]});
            extrude(context, id + "F75", {"entities" : qUnion([Q0]), "depth" : 6 * mm});
        }
        {
            var Q0;
            Q0=sQuery(id+"F74.wireOp",VERTEX,"E216.center");
            var Q1;
            Q1=sQuery(id+"F74.wireOp",VERTEX,"E217.center");
            var Q2;
            Q2=makeQuery(id+"F75.opExtrude","SWEPT_BODY",BODY,{"disambiguationData":[OSD([sQuery(id+"F74.wireOp",EDGE,"E216"),sQuery(id+"F74.wireOp",EDGE,"E217"),sQuery(id+"F74.wireOp",EDGE,"E218.bottom"),sQuery(id+"F74.wireOp",EDGE,"E218.top"),sQuery(id+"F74.wireOp",EDGE,"E218.left"),sQuery(id+"F74.wireOp",EDGE,"E218.right"),sQuery(id+"F74.wireOp",EDGE,"E219"),sQuery(id+"F74.wireOp",EDGE,"E220"),sQuery(id+"F74.wireOp",EDGE,"E221.trimOffspring"),sQuery(id+"F74.wireOp",EDGE,"E222.trimOffspring"),sQuery(id+"F74.wireOp",EDGE,"E223.trimOffspring"),sQuery(id+"F74.wireOp",EDGE,"E224.trimOffspring")])]});
            hole(context, id + "F76", {"style" : HoleStyle.SIMPLE, "endStyle" : HoleEndStyle.THROUGH, "oppositeDirection" : true, "standardTappedOrClearance" : lookupTablePath({ "standard" : "ISO", "engagement" : "25%", "pitch" : "0.6 mm", "size" : "M3", "type" : "Tapped" }), "standardBlindInLast" : lookupTablePath({ "standard" : "ISO", "engagement" : "25%", "pitch" : "0.6 mm", "size" : "M3", "type" : "Tapped" }), "holeDiameter" : 2.6 * mm, "locations" : qUnion([Q0, Q1]), "scope" : qUnion([Q2]), "isTappedThrough" : true, "showTappedDepth" : true});
        }
        {
            var Q0;
            Q0=qCreatedBy(makeId("Top.planeOp"),FACE);
            var sketch = newSketch(context, id + "F77", { "sketchPlane" : qUnion([Q0])});
            skLineSegment(sketch, "E225.bottom", {"start": v(-227.55, 238.49) * mm, "end": v(-215.55, 238.49) * mm});
            skLineSegment(sketch, "E225.top", {"start": v(-227.55, 194.49) * mm, "end": v(-215.55, 194.49) * mm});
            skLineSegment(sketch, "E225.left", {"start": v(-227.55, 238.49) * mm, "end": v(-227.55, 194.49) * mm});
            skLineSegment(sketch, "E225.right", {"start": v(-212.55, 235.49) * mm, "end": v(-212.55, 197.49) * mm});
            skPoint(sketch, "E226", {"position": v(-220.05, 228.49) * mm});
            skPoint(sketch, "E227", {"position": v(-220.05, 204.49) * mm});
            skPoint(sketch, "E228.visualSharp", {"position": v(-212.55, 238.49) * mm});
            skArc(sketch, "E228.filletArc", {"start": v(-212.55, 235.49) * mm, "mid": v(-213.43, 237.6) * mm, "end": v(-215.55, 238.49) * mm});
            skPoint(sketch, "E229.visualSharp", {"position": v(-212.55, 194.49) * mm});
            skArc(sketch, "E229.filletArc", {"start": v(-215.55, 194.49) * mm, "mid": v(-213.43, 195.37) * mm, "end": v(-212.55, 197.49) * mm});
            skCircle(sketch, "E230", {"center": v(-220.05, 228.49) * mm, "radius": 2.5 * mm});
            skCircle(sketch, "E231", {"center": v(-220.05, 204.49) * mm, "radius": 2.5 * mm});
            skSolve(sketch);
        }
        {
            var Q0;
            Q0=makeQuery(id+"F77.imprint","IMPRINT",FACE,{"disambiguationData":[TD([[makeQuery(id+"F77.imprint","IMPRINT",EDGE,{"derivedFrom":sQuery(id+"F77.wireOp",EDGE,"E225.bottom")}),-1.0]])]});
            extrude(context, id + "F78", {"entities" : qUnion([Q0]), "depth" : 6 * mm});
        }
        {
            var Q0;
            Q0=qCreatedBy(makeId("Top.planeOp"),FACE);
            var sketch = newSketch(context, id + "F79", { "sketchPlane" : qUnion([Q0])});
            skLineSegment(sketch, "E232.bottom", {"start": v(-209.45, 237.94) * mm, "end": v(-197.45, 237.94) * mm});
            skLineSegment(sketch, "E232.top", {"start": v(-209.45, 193.94) * mm, "end": v(-197.45, 193.94) * mm});
            skLineSegment(sketch, "E232.left", {"start": v(-209.45, 237.94) * mm, "end": v(-209.45, 193.94) * mm});
            skLineSegment(sketch, "E232.right", {"start": v(-194.45, 234.94) * mm, "end": v(-194.45, 196.94) * mm});
            skPoint(sketch, "E233", {"position": v(-201.95, 227.94) * mm});
            skPoint(sketch, "E234", {"position": v(-201.95, 203.94) * mm});
            skPoint(sketch, "E235.visualSharp", {"position": v(-194.45, 237.94) * mm});
            skArc(sketch, "E235.filletArc", {"start": v(-194.45, 234.94) * mm, "mid": v(-195.33, 237.06) * mm, "end": v(-197.45, 237.94) * mm});
            skPoint(sketch, "E236.visualSharp", {"position": v(-194.45, 193.94) * mm});
            skArc(sketch, "E236.filletArc", {"start": v(-197.45, 193.94) * mm, "mid": v(-195.33, 194.82) * mm, "end": v(-194.45, 196.94) * mm});
            skCircle(sketch, "E237", {"center": v(-201.95, 227.94) * mm, "radius": 2.5 * mm});
            skCircle(sketch, "E238", {"center": v(-201.95, 203.94) * mm, "radius": 2.5 * mm});
            skSolve(sketch);
        }
        {
            var Q0;
            Q0=makeQuery(id+"F79.imprint","IMPRINT",FACE,{"disambiguationData":[TD([[makeQuery(id+"F79.imprint","IMPRINT",EDGE,{"derivedFrom":sQuery(id+"F79.wireOp",EDGE,"E232.bottom")}),-1.0]])]});
            extrude(context, id + "F80", {"entities" : qUnion([Q0]), "depth" : 6 * mm});
        }
        {
            var Q0;
            Q0=qCreatedBy(makeId("Top.planeOp"),FACE);
            var sketch = newSketch(context, id + "F81", { "sketchPlane" : qUnion([Q0])});
            skLineSegment(sketch, "E239.bottom", {"start": v(-191.65, 238.08) * mm, "end": v(-179.65, 238.08) * mm});
            skLineSegment(sketch, "E239.top", {"start": v(-191.65, 194.08) * mm, "end": v(-179.65, 194.08) * mm});
            skLineSegment(sketch, "E239.left", {"start": v(-191.65, 238.08) * mm, "end": v(-191.65, 194.08) * mm});
            skLineSegment(sketch, "E239.right", {"start": v(-176.65, 235.08) * mm, "end": v(-176.65, 197.08) * mm});
            skPoint(sketch, "E240", {"position": v(-184.15, 228.08) * mm});
            skPoint(sketch, "E241", {"position": v(-184.15, 204.08) * mm});
            skPoint(sketch, "E242.visualSharp", {"position": v(-176.65, 238.08) * mm});
            skArc(sketch, "E242.filletArc", {"start": v(-176.65, 235.08) * mm, "mid": v(-177.53, 237.2) * mm, "end": v(-179.65, 238.08) * mm});
            skPoint(sketch, "E243.visualSharp", {"position": v(-176.65, 194.08) * mm});
            skArc(sketch, "E243.filletArc", {"start": v(-179.65, 194.08) * mm, "mid": v(-177.53, 194.96) * mm, "end": v(-176.65, 197.08) * mm});
            skCircle(sketch, "E244", {"center": v(-184.15, 228.08) * mm, "radius": 2.5 * mm});
            skCircle(sketch, "E245", {"center": v(-184.15, 204.08) * mm, "radius": 2.5 * mm});
            skSolve(sketch);
        }
        {
            var Q0;
            Q0=makeQuery(id+"F81.imprint","IMPRINT",FACE,{"disambiguationData":[TD([[makeQuery(id+"F81.imprint","IMPRINT",EDGE,{"derivedFrom":sQuery(id+"F81.wireOp",EDGE,"E239.bottom")}),-1.0]])]});
            extrude(context, id + "F82", {"entities" : qUnion([Q0]), "depth" : 6 * mm});
        }
        {
            var Q0;
            Q0=qCreatedBy(makeId("Top.planeOp"),FACE);
            var sketch = newSketch(context, id + "F83", { "sketchPlane" : qUnion([Q0])});
            skLineSegment(sketch, "E246.bottom", {"start": v(-173.95, 238.22) * mm, "end": v(-161.95, 238.22) * mm});
            skLineSegment(sketch, "E246.top", {"start": v(-173.95, 194.22) * mm, "end": v(-161.95, 194.22) * mm});
            skLineSegment(sketch, "E246.left", {"start": v(-173.95, 238.22) * mm, "end": v(-173.95, 194.22) * mm});
            skLineSegment(sketch, "E246.right", {"start": v(-158.95, 235.22) * mm, "end": v(-158.95, 197.22) * mm});
            skPoint(sketch, "E247", {"position": v(-166.45, 228.22) * mm});
            skPoint(sketch, "E248", {"position": v(-166.45, 204.22) * mm});
            skPoint(sketch, "E249.visualSharp", {"position": v(-158.95, 238.22) * mm});
            skArc(sketch, "E249.filletArc", {"start": v(-158.95, 235.22) * mm, "mid": v(-159.83, 237.34) * mm, "end": v(-161.95, 238.22) * mm});
            skPoint(sketch, "E250.visualSharp", {"position": v(-158.95, 194.22) * mm});
            skArc(sketch, "E250.filletArc", {"start": v(-161.95, 194.22) * mm, "mid": v(-159.83, 195.1) * mm, "end": v(-158.95, 197.22) * mm});
            skCircle(sketch, "E251", {"center": v(-166.45, 228.22) * mm, "radius": 2.5 * mm});
            skCircle(sketch, "E252", {"center": v(-166.45, 204.22) * mm, "radius": 2.5 * mm});
            skSolve(sketch);
        }
        {
            var Q0;
            Q0=makeQuery(id+"F83.imprint","IMPRINT",FACE,{"disambiguationData":[TD([[makeQuery(id+"F83.imprint","IMPRINT",EDGE,{"derivedFrom":sQuery(id+"F83.wireOp",EDGE,"E246.bottom")}),-1.0]])]});
            extrude(context, id + "F84", {"entities" : qUnion([Q0]), "depth" : 6 * mm});
        }
        {
            var Q0;
            Q0=makeQuery(id+"F68.opExtrude","SWEPT_BODY",BODY,{"disambiguationData":[OSD([sQuery(id+"F67.wireOp",EDGE,"E205.bottom"),sQuery(id+"F67.wireOp",EDGE,"E205.top"),sQuery(id+"F67.wireOp",EDGE,"E205.left"),sQuery(id+"F67.wireOp",EDGE,"E205.right")])]});
            deleteBodies(context, id + "F85", {"entities" : qUnion([Q0])});
        }
    });
